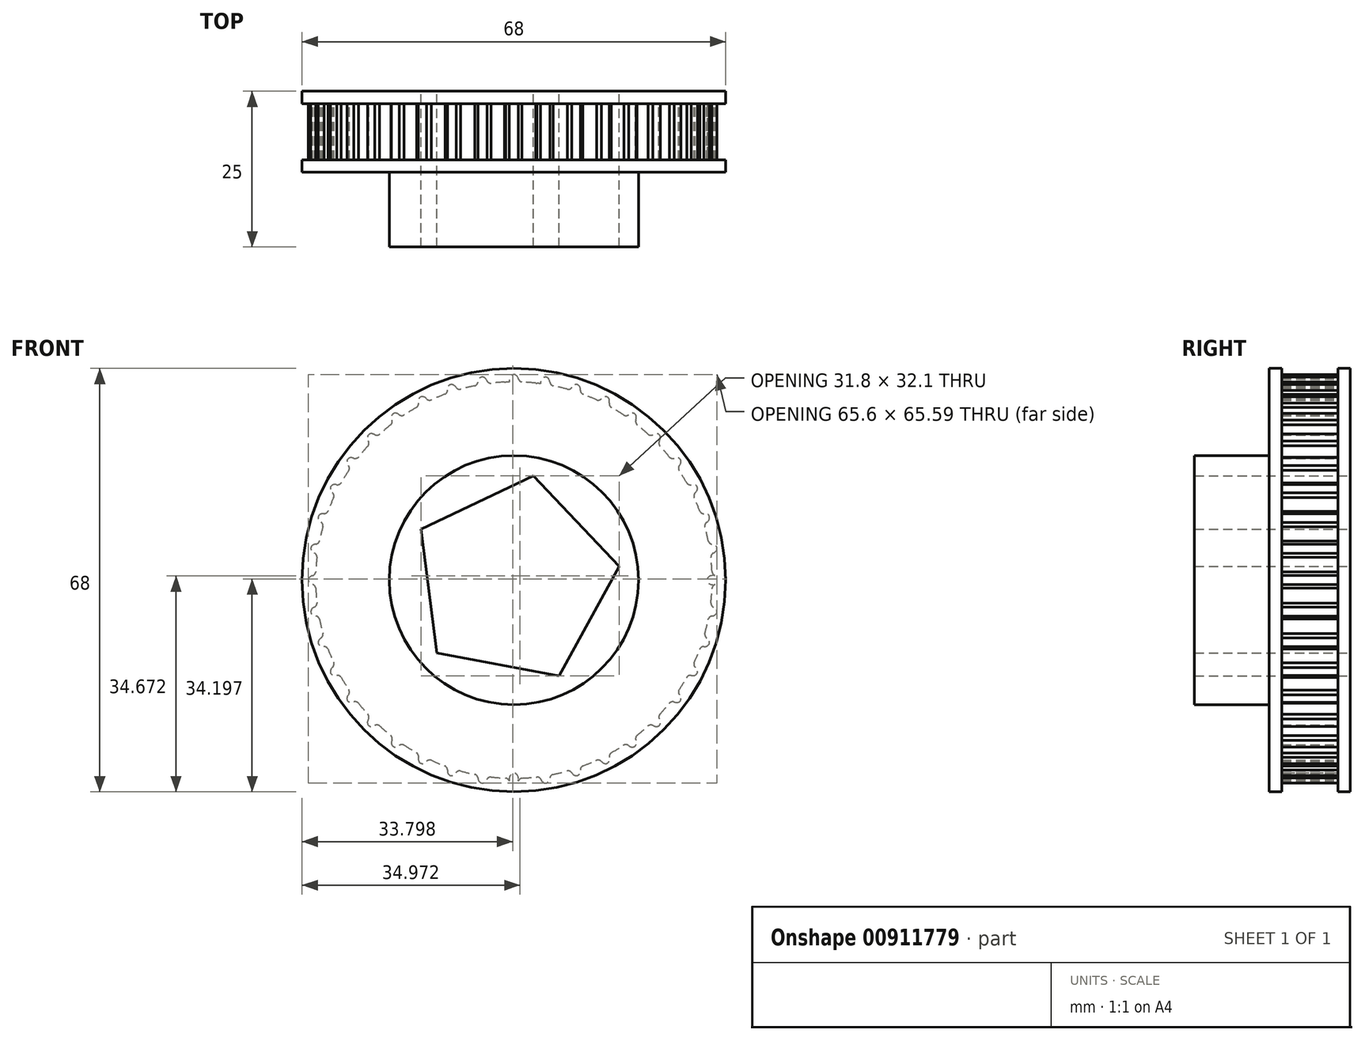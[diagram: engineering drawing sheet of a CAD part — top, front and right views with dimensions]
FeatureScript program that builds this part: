
annotation { "Feature Type Name" : "Feature", "Feature Type Description" : "" }
export const myFeature = defineFeature(function(context is Context, id is Id, definition is map)
    precondition{}
    {
        {
            var Q0;
            Q0=qCreatedBy(makeId("Front.planeOp"),FACE);
            var sketch = newSketch(context, id + "F0", { "sketchPlane" : qUnion([Q0])});
            skCircle(sketch, "E0", {"center": v(0, 0) * mm, "radius": 31.83 * mm});
            skEllipse(sketch, "E1", {"center": v(0, 32) * mm, "majorRadius": 1 * mm, "minorRadius": 0.76 * mm, "majorAxis": v(0, 1)});
            skArc(sketch, "E2", {"start": v(-1.5, 31.8) * mm, "mid": v(-1.02, 31.91) * mm, "end": v(-0.72, 32.3) * mm});
            skArc(sketch, "E3", {"start": v(0.73, 32.28) * mm, "mid": v(1.02, 31.92) * mm, "end": v(1.47, 31.8) * mm});
            skArc(sketch, "E4.1.0", {"start": v(-6.45, 31.17) * mm, "mid": v(-6, 31.36) * mm, "end": v(-5.76, 31.8) * mm});
            skEllipse(sketch, "E4.1.1", {"center": v(-5, 31.6) * mm, "majorRadius": 1 * mm, "minorRadius": 0.76 * mm, "majorAxis": v(-0.16, 0.99)});
            skArc(sketch, "E4.1.2", {"start": v(-4.33, 32) * mm, "mid": v(-3.99, 31.68) * mm, "end": v(-3.52, 31.63) * mm});
            skArc(sketch, "E4.2.0", {"start": v(-11.25, 29.78) * mm, "mid": v(-10.83, 30.04) * mm, "end": v(-10.67, 30.5) * mm});
            skEllipse(sketch, "E4.2.1", {"center": v(-9.89, 30.44) * mm, "majorRadius": 1 * mm, "minorRadius": 0.76 * mm, "majorAxis": v(-0.3, 0.95)});
            skArc(sketch, "E4.2.2", {"start": v(-9.28, 30.93) * mm, "mid": v(-8.9, 30.67) * mm, "end": v(-8.43, 30.7) * mm});
            skArc(sketch, "E4.3.0", {"start": v(-15.77, 27.65) * mm, "mid": v(-15.4, 27.97) * mm, "end": v(-15.3, 28.46) * mm});
            skEllipse(sketch, "E4.3.1", {"center": v(-14.53, 28.52) * mm, "majorRadius": 1 * mm, "minorRadius": 0.76 * mm, "majorAxis": v(-0.45, 0.9)});
            skArc(sketch, "E4.3.2", {"start": v(-14, 29.1) * mm, "mid": v(-13.58, 28.9) * mm, "end": v(-13.12, 29) * mm});
            skArc(sketch, "E4.4.0", {"start": v(-19.9, 24.84) * mm, "mid": v(-19.58, 25.22) * mm, "end": v(-19.57, 25.71) * mm});
            skEllipse(sketch, "E4.4.1", {"center": v(-18.8, 25.9) * mm, "majorRadius": 1 * mm, "minorRadius": 0.76 * mm, "majorAxis": v(-0.59, 0.8)});
            skArc(sketch, "E4.4.2", {"start": v(-18.39, 26.54) * mm, "mid": v(-17.93, 26.42) * mm, "end": v(-17.5, 26.59) * mm});
            skArc(sketch, "E4.5.0", {"start": v(-23.54, 21.42) * mm, "mid": v(-23.29, 21.85) * mm, "end": v(-23.35, 22.33) * mm});
            skEllipse(sketch, "E4.5.1", {"center": v(-22.63, 22.63) * mm, "majorRadius": 1 * mm, "minorRadius": 0.76 * mm, "majorAxis": v(-0.7, 0.7)});
            skArc(sketch, "E4.5.2", {"start": v(-22.31, 23.34) * mm, "mid": v(-21.85, 23.29) * mm, "end": v(-21.44, 23.52) * mm});
            skArc(sketch, "E4.6.0", {"start": v(-26.6, 17.48) * mm, "mid": v(-26.42, 17.93) * mm, "end": v(-26.56, 18.4) * mm});
            skEllipse(sketch, "E4.6.1", {"center": v(-25.9, 18.81) * mm, "majorRadius": 1 * mm, "minorRadius": 0.76 * mm, "majorAxis": v(-0.8, 0.59)});
            skArc(sketch, "E4.6.2", {"start": v(-25.69, 19.56) * mm, "mid": v(-25.22, 19.58) * mm, "end": v(-24.86, 19.88) * mm});
            skArc(sketch, "E4.7.0", {"start": v(-29, 13.1) * mm, "mid": v(-28.9, 13.58) * mm, "end": v(-29.1, 14.03) * mm});
            skEllipse(sketch, "E4.7.1", {"center": v(-28.51, 14.53) * mm, "majorRadius": 1 * mm, "minorRadius": 0.76 * mm, "majorAxis": v(-0.9, 0.45)});
            skArc(sketch, "E4.7.2", {"start": v(-28.43, 15.3) * mm, "mid": v(-27.97, 15.4) * mm, "end": v(-27.66, 15.75) * mm});
            skArc(sketch, "E4.8.0", {"start": v(-30.7, 8.4) * mm, "mid": v(-30.67, 8.9) * mm, "end": v(-30.94, 9.3) * mm});
            skEllipse(sketch, "E4.8.1", {"center": v(-30.44, 9.9) * mm, "majorRadius": 1 * mm, "minorRadius": 0.76 * mm, "majorAxis": v(-0.95, 0.3)});
            skArc(sketch, "E4.8.2", {"start": v(-30.48, 10.67) * mm, "mid": v(-30.04, 10.83) * mm, "end": v(-29.78, 11.22) * mm});
            skArc(sketch, "E4.9.0", {"start": v(-31.64, 3.5) * mm, "mid": v(-31.68, 3.99) * mm, "end": v(-32.02, 4.34) * mm});
            skEllipse(sketch, "E4.9.1", {"center": v(-31.6, 5) * mm, "majorRadius": 1 * mm, "minorRadius": 0.76 * mm, "majorAxis": v(-0.99, 0.16)});
            skArc(sketch, "E4.9.2", {"start": v(-31.77, 5.77) * mm, "mid": v(-31.36, 6) * mm, "end": v(-31.17, 6.43) * mm});
            skArc(sketch, "E4.10.0", {"start": v(-31.8, -1.5) * mm, "mid": v(-31.91, -1.02) * mm, "end": v(-32.3, -0.72) * mm});
            skEllipse(sketch, "E4.10.1", {"center": v(-32, 0) * mm, "majorRadius": 1 * mm, "minorRadius": 0.76 * mm, "majorAxis": v(-1, 0)});
            skArc(sketch, "E4.10.2", {"start": v(-32.28, 0.73) * mm, "mid": v(-31.92, 1.02) * mm, "end": v(-31.8, 1.47) * mm});
            skArc(sketch, "E4.11.0", {"start": v(-31.17, -6.45) * mm, "mid": v(-31.36, -6) * mm, "end": v(-31.8, -5.76) * mm});
            skEllipse(sketch, "E4.11.1", {"center": v(-31.6, -5) * mm, "majorRadius": 1 * mm, "minorRadius": 0.76 * mm, "majorAxis": v(-0.99, -0.16)});
            skArc(sketch, "E4.11.2", {"start": v(-32, -4.33) * mm, "mid": v(-31.68, -3.99) * mm, "end": v(-31.63, -3.52) * mm});
            skArc(sketch, "E4.12.0", {"start": v(-29.78, -11.25) * mm, "mid": v(-30.04, -10.83) * mm, "end": v(-30.5, -10.67) * mm});
            skEllipse(sketch, "E4.12.1", {"center": v(-30.44, -9.89) * mm, "majorRadius": 1 * mm, "minorRadius": 0.76 * mm, "majorAxis": v(-0.95, -0.3)});
            skArc(sketch, "E4.12.2", {"start": v(-30.93, -9.28) * mm, "mid": v(-30.67, -8.9) * mm, "end": v(-30.7, -8.43) * mm});
            skArc(sketch, "E4.13.0", {"start": v(-27.65, -15.77) * mm, "mid": v(-27.97, -15.4) * mm, "end": v(-28.46, -15.3) * mm});
            skEllipse(sketch, "E4.13.1", {"center": v(-28.52, -14.53) * mm, "majorRadius": 1 * mm, "minorRadius": 0.76 * mm, "majorAxis": v(-0.9, -0.45)});
            skArc(sketch, "E4.13.2", {"start": v(-29.1, -14) * mm, "mid": v(-28.9, -13.58) * mm, "end": v(-29, -13.12) * mm});
            skArc(sketch, "E4.14.0", {"start": v(-24.84, -19.9) * mm, "mid": v(-25.22, -19.58) * mm, "end": v(-25.71, -19.57) * mm});
            skEllipse(sketch, "E4.14.1", {"center": v(-25.9, -18.8) * mm, "majorRadius": 1 * mm, "minorRadius": 0.76 * mm, "majorAxis": v(-0.8, -0.59)});
            skArc(sketch, "E4.14.2", {"start": v(-26.54, -18.39) * mm, "mid": v(-26.42, -17.93) * mm, "end": v(-26.59, -17.5) * mm});
            skArc(sketch, "E4.15.0", {"start": v(-21.42, -23.54) * mm, "mid": v(-21.85, -23.29) * mm, "end": v(-22.33, -23.35) * mm});
            skEllipse(sketch, "E4.15.1", {"center": v(-22.63, -22.63) * mm, "majorRadius": 1 * mm, "minorRadius": 0.76 * mm, "majorAxis": v(-0.7, -0.7)});
            skArc(sketch, "E4.15.2", {"start": v(-23.34, -22.31) * mm, "mid": v(-23.29, -21.85) * mm, "end": v(-23.52, -21.44) * mm});
            skArc(sketch, "E4.16.0", {"start": v(-17.48, -26.6) * mm, "mid": v(-17.93, -26.42) * mm, "end": v(-18.4, -26.56) * mm});
            skEllipse(sketch, "E4.16.1", {"center": v(-18.81, -25.9) * mm, "majorRadius": 1 * mm, "minorRadius": 0.76 * mm, "majorAxis": v(-0.59, -0.8)});
            skArc(sketch, "E4.16.2", {"start": v(-19.56, -25.69) * mm, "mid": v(-19.58, -25.22) * mm, "end": v(-19.88, -24.86) * mm});
            skArc(sketch, "E4.17.0", {"start": v(-13.1, -29) * mm, "mid": v(-13.58, -28.9) * mm, "end": v(-14.03, -29.1) * mm});
            skEllipse(sketch, "E4.17.1", {"center": v(-14.53, -28.51) * mm, "majorRadius": 1 * mm, "minorRadius": 0.76 * mm, "majorAxis": v(-0.45, -0.9)});
            skArc(sketch, "E4.17.2", {"start": v(-15.3, -28.43) * mm, "mid": v(-15.4, -27.97) * mm, "end": v(-15.75, -27.66) * mm});
            skArc(sketch, "E4.18.0", {"start": v(-8.4, -30.7) * mm, "mid": v(-8.9, -30.67) * mm, "end": v(-9.3, -30.94) * mm});
            skEllipse(sketch, "E4.18.1", {"center": v(-9.9, -30.44) * mm, "majorRadius": 1 * mm, "minorRadius": 0.76 * mm, "majorAxis": v(-0.3, -0.95)});
            skArc(sketch, "E4.18.2", {"start": v(-10.67, -30.48) * mm, "mid": v(-10.83, -30.04) * mm, "end": v(-11.22, -29.78) * mm});
            skArc(sketch, "E4.19.0", {"start": v(-3.5, -31.64) * mm, "mid": v(-3.99, -31.68) * mm, "end": v(-4.34, -32.02) * mm});
            skEllipse(sketch, "E4.19.1", {"center": v(-5, -31.6) * mm, "majorRadius": 1 * mm, "minorRadius": 0.76 * mm, "majorAxis": v(-0.16, -0.99)});
            skArc(sketch, "E4.19.2", {"start": v(-5.77, -31.77) * mm, "mid": v(-6, -31.36) * mm, "end": v(-6.43, -31.17) * mm});
            skArc(sketch, "E4.20.0", {"start": v(1.5, -31.8) * mm, "mid": v(1.02, -31.91) * mm, "end": v(0.72, -32.3) * mm});
            skEllipse(sketch, "E4.20.1", {"center": v(0, -32) * mm, "majorRadius": 1 * mm, "minorRadius": 0.76 * mm, "majorAxis": v(0, -1)});
            skArc(sketch, "E4.20.2", {"start": v(-0.73, -32.28) * mm, "mid": v(-1.02, -31.92) * mm, "end": v(-1.47, -31.8) * mm});
            skArc(sketch, "E4.21.0", {"start": v(6.45, -31.17) * mm, "mid": v(6, -31.36) * mm, "end": v(5.76, -31.8) * mm});
            skEllipse(sketch, "E4.21.1", {"center": v(5, -31.6) * mm, "majorRadius": 1 * mm, "minorRadius": 0.76 * mm, "majorAxis": v(0.16, -0.99)});
            skArc(sketch, "E4.21.2", {"start": v(4.33, -32) * mm, "mid": v(3.99, -31.68) * mm, "end": v(3.52, -31.63) * mm});
            skArc(sketch, "E4.22.0", {"start": v(11.25, -29.78) * mm, "mid": v(10.83, -30.04) * mm, "end": v(10.67, -30.5) * mm});
            skEllipse(sketch, "E4.22.1", {"center": v(9.89, -30.44) * mm, "majorRadius": 1 * mm, "minorRadius": 0.76 * mm, "majorAxis": v(0.3, -0.95)});
            skArc(sketch, "E4.22.2", {"start": v(9.28, -30.93) * mm, "mid": v(8.9, -30.67) * mm, "end": v(8.43, -30.7) * mm});
            skArc(sketch, "E4.23.0", {"start": v(15.77, -27.65) * mm, "mid": v(15.4, -27.97) * mm, "end": v(15.3, -28.46) * mm});
            skEllipse(sketch, "E4.23.1", {"center": v(14.53, -28.52) * mm, "majorRadius": 1 * mm, "minorRadius": 0.76 * mm, "majorAxis": v(0.45, -0.9)});
            skArc(sketch, "E4.23.2", {"start": v(14, -29.1) * mm, "mid": v(13.58, -28.9) * mm, "end": v(13.12, -29) * mm});
            skArc(sketch, "E4.24.0", {"start": v(19.9, -24.84) * mm, "mid": v(19.58, -25.22) * mm, "end": v(19.57, -25.71) * mm});
            skEllipse(sketch, "E4.24.1", {"center": v(18.8, -25.9) * mm, "majorRadius": 1 * mm, "minorRadius": 0.76 * mm, "majorAxis": v(0.59, -0.8)});
            skArc(sketch, "E4.24.2", {"start": v(18.39, -26.54) * mm, "mid": v(17.93, -26.42) * mm, "end": v(17.5, -26.59) * mm});
            skArc(sketch, "E4.25.0", {"start": v(23.54, -21.42) * mm, "mid": v(23.29, -21.85) * mm, "end": v(23.35, -22.33) * mm});
            skEllipse(sketch, "E4.25.1", {"center": v(22.63, -22.63) * mm, "majorRadius": 1 * mm, "minorRadius": 0.76 * mm, "majorAxis": v(0.7, -0.7)});
            skArc(sketch, "E4.25.2", {"start": v(22.31, -23.34) * mm, "mid": v(21.85, -23.29) * mm, "end": v(21.44, -23.52) * mm});
            skArc(sketch, "E4.26.0", {"start": v(26.6, -17.48) * mm, "mid": v(26.42, -17.93) * mm, "end": v(26.56, -18.4) * mm});
            skEllipse(sketch, "E4.26.1", {"center": v(25.9, -18.81) * mm, "majorRadius": 1 * mm, "minorRadius": 0.76 * mm, "majorAxis": v(0.8, -0.59)});
            skArc(sketch, "E4.26.2", {"start": v(25.69, -19.56) * mm, "mid": v(25.22, -19.58) * mm, "end": v(24.86, -19.88) * mm});
            skArc(sketch, "E4.27.0", {"start": v(29, -13.1) * mm, "mid": v(28.9, -13.58) * mm, "end": v(29.1, -14.03) * mm});
            skEllipse(sketch, "E4.27.1", {"center": v(28.51, -14.53) * mm, "majorRadius": 1 * mm, "minorRadius": 0.76 * mm, "majorAxis": v(0.9, -0.45)});
            skArc(sketch, "E4.27.2", {"start": v(28.43, -15.3) * mm, "mid": v(27.97, -15.4) * mm, "end": v(27.66, -15.75) * mm});
            skArc(sketch, "E4.28.0", {"start": v(30.7, -8.4) * mm, "mid": v(30.67, -8.9) * mm, "end": v(30.94, -9.3) * mm});
            skEllipse(sketch, "E4.28.1", {"center": v(30.44, -9.9) * mm, "majorRadius": 1 * mm, "minorRadius": 0.76 * mm, "majorAxis": v(0.95, -0.3)});
            skArc(sketch, "E4.28.2", {"start": v(30.48, -10.67) * mm, "mid": v(30.04, -10.83) * mm, "end": v(29.78, -11.22) * mm});
            skArc(sketch, "E4.29.0", {"start": v(31.64, -3.5) * mm, "mid": v(31.68, -3.99) * mm, "end": v(32.02, -4.34) * mm});
            skEllipse(sketch, "E4.29.1", {"center": v(31.6, -5) * mm, "majorRadius": 1 * mm, "minorRadius": 0.76 * mm, "majorAxis": v(0.99, -0.16)});
            skArc(sketch, "E4.29.2", {"start": v(31.77, -5.77) * mm, "mid": v(31.36, -6) * mm, "end": v(31.17, -6.43) * mm});
            skArc(sketch, "E4.30.0", {"start": v(31.8, 1.5) * mm, "mid": v(31.91, 1.02) * mm, "end": v(32.3, 0.72) * mm});
            skEllipse(sketch, "E4.30.1", {"center": v(32, 0) * mm, "majorRadius": 1 * mm, "minorRadius": 0.76 * mm, "majorAxis": v(1, 0)});
            skArc(sketch, "E4.30.2", {"start": v(32.28, -0.73) * mm, "mid": v(31.92, -1.02) * mm, "end": v(31.8, -1.47) * mm});
            skArc(sketch, "E4.31.0", {"start": v(31.17, 6.45) * mm, "mid": v(31.36, 6) * mm, "end": v(31.8, 5.76) * mm});
            skEllipse(sketch, "E4.31.1", {"center": v(31.6, 5) * mm, "majorRadius": 1 * mm, "minorRadius": 0.76 * mm, "majorAxis": v(0.99, 0.16)});
            skArc(sketch, "E4.31.2", {"start": v(32, 4.33) * mm, "mid": v(31.68, 3.99) * mm, "end": v(31.63, 3.52) * mm});
            skArc(sketch, "E4.32.0", {"start": v(29.78, 11.25) * mm, "mid": v(30.04, 10.83) * mm, "end": v(30.5, 10.67) * mm});
            skEllipse(sketch, "E4.32.1", {"center": v(30.44, 9.89) * mm, "majorRadius": 1 * mm, "minorRadius": 0.76 * mm, "majorAxis": v(0.95, 0.3)});
            skArc(sketch, "E4.32.2", {"start": v(30.93, 9.28) * mm, "mid": v(30.67, 8.9) * mm, "end": v(30.7, 8.43) * mm});
            skArc(sketch, "E4.33.0", {"start": v(27.65, 15.77) * mm, "mid": v(27.97, 15.4) * mm, "end": v(28.46, 15.3) * mm});
            skEllipse(sketch, "E4.33.1", {"center": v(28.52, 14.53) * mm, "majorRadius": 1 * mm, "minorRadius": 0.76 * mm, "majorAxis": v(0.9, 0.45)});
            skArc(sketch, "E4.33.2", {"start": v(29.1, 14) * mm, "mid": v(28.9, 13.58) * mm, "end": v(29, 13.12) * mm});
            skArc(sketch, "E4.34.0", {"start": v(24.84, 19.9) * mm, "mid": v(25.22, 19.58) * mm, "end": v(25.71, 19.57) * mm});
            skEllipse(sketch, "E4.34.1", {"center": v(25.9, 18.8) * mm, "majorRadius": 1 * mm, "minorRadius": 0.76 * mm, "majorAxis": v(0.8, 0.59)});
            skArc(sketch, "E4.34.2", {"start": v(26.54, 18.39) * mm, "mid": v(26.42, 17.93) * mm, "end": v(26.59, 17.5) * mm});
            skArc(sketch, "E4.35.0", {"start": v(21.42, 23.54) * mm, "mid": v(21.85, 23.29) * mm, "end": v(22.33, 23.35) * mm});
            skEllipse(sketch, "E4.35.1", {"center": v(22.63, 22.63) * mm, "majorRadius": 1 * mm, "minorRadius": 0.76 * mm, "majorAxis": v(0.7, 0.7)});
            skArc(sketch, "E4.35.2", {"start": v(23.34, 22.31) * mm, "mid": v(23.29, 21.85) * mm, "end": v(23.52, 21.44) * mm});
            skArc(sketch, "E4.36.0", {"start": v(17.48, 26.6) * mm, "mid": v(17.93, 26.42) * mm, "end": v(18.4, 26.56) * mm});
            skEllipse(sketch, "E4.36.1", {"center": v(18.81, 25.9) * mm, "majorRadius": 1 * mm, "minorRadius": 0.76 * mm, "majorAxis": v(0.59, 0.8)});
            skArc(sketch, "E4.36.2", {"start": v(19.56, 25.69) * mm, "mid": v(19.58, 25.22) * mm, "end": v(19.88, 24.86) * mm});
            skArc(sketch, "E4.37.0", {"start": v(13.1, 29) * mm, "mid": v(13.58, 28.9) * mm, "end": v(14.03, 29.1) * mm});
            skEllipse(sketch, "E4.37.1", {"center": v(14.53, 28.51) * mm, "majorRadius": 1 * mm, "minorRadius": 0.76 * mm, "majorAxis": v(0.45, 0.9)});
            skArc(sketch, "E4.37.2", {"start": v(15.3, 28.43) * mm, "mid": v(15.4, 27.97) * mm, "end": v(15.75, 27.66) * mm});
            skArc(sketch, "E4.38.0", {"start": v(8.4, 30.7) * mm, "mid": v(8.9, 30.67) * mm, "end": v(9.3, 30.94) * mm});
            skEllipse(sketch, "E4.38.1", {"center": v(9.9, 30.44) * mm, "majorRadius": 1 * mm, "minorRadius": 0.76 * mm, "majorAxis": v(0.3, 0.95)});
            skArc(sketch, "E4.38.2", {"start": v(10.67, 30.48) * mm, "mid": v(10.83, 30.04) * mm, "end": v(11.22, 29.78) * mm});
            skArc(sketch, "E4.39.0", {"start": v(3.5, 31.64) * mm, "mid": v(3.99, 31.68) * mm, "end": v(4.34, 32.02) * mm});
            skEllipse(sketch, "E4.39.1", {"center": v(5, 31.6) * mm, "majorRadius": 1 * mm, "minorRadius": 0.76 * mm, "majorAxis": v(0.16, 0.99)});
            skArc(sketch, "E4.39.2", {"start": v(5.77, 31.77) * mm, "mid": v(6, 31.36) * mm, "end": v(6.43, 31.17) * mm});
            skSolve(sketch);
        }
        {
            var Q0;
            {var subQ0=sQuery(id+"F0.wireOp",EDGE,"E4.9.1");var subQ1=sQuery(id+"F0.wireOp",EDGE,"E0");var subQ2=makeQuery(id+"F0.imprint","INTERSECT",VERTEX,{"disambiguationData":[OD(0.0)],"derivedFrom":[subQ1,subQ0]});Q0=makeQuery(id+"F0.imprint","IMPRINT",FACE,{"disambiguationData":[TD([[makeQuery(id+"F0.imprint","IMPRINT",EDGE,{"disambiguationData":[TD([[subQ2,-1.0]])],"derivedFrom":subQ1}),-1.0]])]});}
            var Q1;
            {var subQ1=sQuery(id+"F0.wireOp",EDGE,"E0");var subQ208=sQuery(id+"F0.wireOp",EDGE,"E4.30.0");var subQ210=makeQuery(id+"F0.imprint","INTERSECT",VERTEX,{"disambiguationData":[OD(1.0)],"derivedFrom":[subQ1,subQ208]});Q1=makeQuery(id+"F0.imprint","IMPRINT",FACE,{"disambiguationData":[TD([[makeQuery(id+"F0.imprint","IMPRINT",EDGE,{"disambiguationData":[TD([[subQ210,1.0]])],"derivedFrom":subQ1}),1.0]])]});}
            var Q2;
            {var subQ0=sQuery(id+"F0.wireOp",EDGE,"E4.4.1");var subQ1=sQuery(id+"F0.wireOp",EDGE,"E0");var subQ2=makeQuery(id+"F0.imprint","INTERSECT",VERTEX,{"disambiguationData":[OD(0.0)],"derivedFrom":[subQ1,subQ0]});Q2=makeQuery(id+"F0.imprint","IMPRINT",FACE,{"disambiguationData":[TD([[makeQuery(id+"F0.imprint","IMPRINT",EDGE,{"disambiguationData":[TD([[subQ2,-1.0]])],"derivedFrom":subQ1}),1.0]])]});}
            var Q3;
            {var subQ0=sQuery(id+"F0.wireOp",EDGE,"E4.8.0");var subQ1=sQuery(id+"F0.wireOp",EDGE,"E0");var subQ2=makeQuery(id+"F0.imprint","INTERSECT",VERTEX,{"disambiguationData":[OD(1.0)],"derivedFrom":[subQ1,subQ0]});Q3=makeQuery(id+"F0.imprint","IMPRINT",FACE,{"disambiguationData":[TD([[makeQuery(id+"F0.imprint","IMPRINT",EDGE,{"disambiguationData":[TD([[subQ2,1.0]])],"derivedFrom":subQ1}),-1.0]])]});}
            var Q4;
            {var subQ0=sQuery(id+"F0.wireOp",EDGE,"E4.32.1");var subQ1=sQuery(id+"F0.wireOp",EDGE,"E0");var subQ2=makeQuery(id+"F0.imprint","INTERSECT",VERTEX,{"disambiguationData":[OD(0.0)],"derivedFrom":[subQ1,subQ0]});Q4=makeQuery(id+"F0.imprint","IMPRINT",FACE,{"disambiguationData":[TD([[makeQuery(id+"F0.imprint","IMPRINT",EDGE,{"disambiguationData":[TD([[subQ2,-1.0]])],"derivedFrom":subQ1}),-1.0]])]});}
            var Q5;
            {var subQ0=sQuery(id+"F0.wireOp",EDGE,"E4.30.1");var subQ1=sQuery(id+"F0.wireOp",EDGE,"E0");var subQ2=makeQuery(id+"F0.imprint","INTERSECT",VERTEX,{"disambiguationData":[OD(0.0)],"derivedFrom":[subQ1,subQ0]});Q5=makeQuery(id+"F0.imprint","IMPRINT",FACE,{"disambiguationData":[TD([[makeQuery(id+"F0.imprint","IMPRINT",EDGE,{"disambiguationData":[TD([[subQ2,1.0]])],"derivedFrom":subQ1}),1.0]])]});}
            var Q6;
            {var subQ0=sQuery(id+"F0.wireOp",EDGE,"E4.36.1");var subQ1=sQuery(id+"F0.wireOp",EDGE,"E0");var subQ2=makeQuery(id+"F0.imprint","INTERSECT",VERTEX,{"disambiguationData":[OD(0.0)],"derivedFrom":[subQ1,subQ0]});Q6=makeQuery(id+"F0.imprint","IMPRINT",FACE,{"disambiguationData":[TD([[makeQuery(id+"F0.imprint","IMPRINT",EDGE,{"disambiguationData":[TD([[subQ2,-1.0]])],"derivedFrom":subQ1}),1.0]])]});}
            var Q7;
            {var subQ0=sQuery(id+"F0.wireOp",EDGE,"E4.10.1");var subQ1=sQuery(id+"F0.wireOp",EDGE,"E0");var subQ2=makeQuery(id+"F0.imprint","INTERSECT",VERTEX,{"disambiguationData":[OD(0.0)],"derivedFrom":[subQ1,subQ0]});Q7=makeQuery(id+"F0.imprint","IMPRINT",FACE,{"disambiguationData":[TD([[makeQuery(id+"F0.imprint","IMPRINT",EDGE,{"disambiguationData":[TD([[subQ2,-1.0]])],"derivedFrom":subQ1}),1.0]])]});}
            var Q8;
            {var subQ0=sQuery(id+"F0.wireOp",EDGE,"E4.6.1");var subQ1=sQuery(id+"F0.wireOp",EDGE,"E0");var subQ2=makeQuery(id+"F0.imprint","INTERSECT",VERTEX,{"disambiguationData":[OD(0.0)],"derivedFrom":[subQ1,subQ0]});Q8=makeQuery(id+"F0.imprint","IMPRINT",FACE,{"disambiguationData":[TD([[makeQuery(id+"F0.imprint","IMPRINT",EDGE,{"disambiguationData":[TD([[subQ2,-1.0]])],"derivedFrom":subQ1}),1.0]])]});}
            var Q9;
            {var subQ0=sQuery(id+"F0.wireOp",EDGE,"E4.26.1");var subQ1=sQuery(id+"F0.wireOp",EDGE,"E0");var subQ2=makeQuery(id+"F0.imprint","INTERSECT",VERTEX,{"disambiguationData":[OD(0.0)],"derivedFrom":[subQ1,subQ0]});Q9=makeQuery(id+"F0.imprint","IMPRINT",FACE,{"disambiguationData":[TD([[makeQuery(id+"F0.imprint","IMPRINT",EDGE,{"disambiguationData":[TD([[subQ2,-1.0]])],"derivedFrom":subQ1}),1.0]])]});}
            var Q10;
            {var subQ0=sQuery(id+"F0.wireOp",EDGE,"E4.21.1");var subQ1=sQuery(id+"F0.wireOp",EDGE,"E0");var subQ2=makeQuery(id+"F0.imprint","INTERSECT",VERTEX,{"disambiguationData":[OD(0.0)],"derivedFrom":[subQ1,subQ0]});Q10=makeQuery(id+"F0.imprint","IMPRINT",FACE,{"disambiguationData":[TD([[makeQuery(id+"F0.imprint","IMPRINT",EDGE,{"disambiguationData":[TD([[subQ2,-1.0]])],"derivedFrom":subQ1}),1.0]])]});}
            var Q11;
            {var subQ0=sQuery(id+"F0.wireOp",EDGE,"E4.18.1");var subQ1=sQuery(id+"F0.wireOp",EDGE,"E0");var subQ2=makeQuery(id+"F0.imprint","INTERSECT",VERTEX,{"disambiguationData":[OD(0.0)],"derivedFrom":[subQ1,subQ0]});Q11=makeQuery(id+"F0.imprint","IMPRINT",FACE,{"disambiguationData":[TD([[makeQuery(id+"F0.imprint","IMPRINT",EDGE,{"disambiguationData":[TD([[subQ2,-1.0]])],"derivedFrom":subQ1}),-1.0]])]});}
            var Q12;
            {var subQ0=sQuery(id+"F0.wireOp",EDGE,"E1");var subQ1=sQuery(id+"F0.wireOp",EDGE,"E0");var subQ2=makeQuery(id+"F0.imprint","INTERSECT",VERTEX,{"disambiguationData":[OD(0.0)],"derivedFrom":[subQ1,subQ0]});Q12=makeQuery(id+"F0.imprint","IMPRINT",FACE,{"disambiguationData":[TD([[makeQuery(id+"F0.imprint","IMPRINT",EDGE,{"disambiguationData":[TD([[subQ2,-1.0]])],"derivedFrom":subQ1}),1.0]])]});}
            var Q13;
            {var subQ0=sQuery(id+"F0.wireOp",EDGE,"E4.33.1");var subQ1=sQuery(id+"F0.wireOp",EDGE,"E0");var subQ2=makeQuery(id+"F0.imprint","INTERSECT",VERTEX,{"disambiguationData":[OD(0.0)],"derivedFrom":[subQ1,subQ0]});Q13=makeQuery(id+"F0.imprint","IMPRINT",FACE,{"disambiguationData":[TD([[makeQuery(id+"F0.imprint","IMPRINT",EDGE,{"disambiguationData":[TD([[subQ2,-1.0]])],"derivedFrom":subQ1}),1.0]])]});}
            var Q14;
            {var subQ0=sQuery(id+"F0.wireOp",EDGE,"E4.34.1");var subQ1=sQuery(id+"F0.wireOp",EDGE,"E0");var subQ2=makeQuery(id+"F0.imprint","INTERSECT",VERTEX,{"disambiguationData":[OD(0.0)],"derivedFrom":[subQ1,subQ0]});Q14=makeQuery(id+"F0.imprint","IMPRINT",FACE,{"disambiguationData":[TD([[makeQuery(id+"F0.imprint","IMPRINT",EDGE,{"disambiguationData":[TD([[subQ2,-1.0]])],"derivedFrom":subQ1}),1.0]])]});}
            var Q15;
            {var subQ0=sQuery(id+"F0.wireOp",EDGE,"E4.17.0");var subQ1=sQuery(id+"F0.wireOp",EDGE,"E0");var subQ2=makeQuery(id+"F0.imprint","INTERSECT",VERTEX,{"disambiguationData":[OD(1.0)],"derivedFrom":[subQ1,subQ0]});Q15=makeQuery(id+"F0.imprint","IMPRINT",FACE,{"disambiguationData":[TD([[makeQuery(id+"F0.imprint","IMPRINT",EDGE,{"disambiguationData":[TD([[subQ2,1.0]])],"derivedFrom":subQ1}),-1.0]])]});}
            var Q16;
            {var subQ0=sQuery(id+"F0.wireOp",EDGE,"E4.39.1");var subQ1=sQuery(id+"F0.wireOp",EDGE,"E0");var subQ2=makeQuery(id+"F0.imprint","INTERSECT",VERTEX,{"disambiguationData":[OD(0.0)],"derivedFrom":[subQ1,subQ0]});Q16=makeQuery(id+"F0.imprint","IMPRINT",FACE,{"disambiguationData":[TD([[makeQuery(id+"F0.imprint","IMPRINT",EDGE,{"disambiguationData":[TD([[subQ2,-1.0]])],"derivedFrom":subQ1}),1.0]])]});}
            var Q17;
            {var subQ0=sQuery(id+"F0.wireOp",EDGE,"E4.7.1");var subQ1=sQuery(id+"F0.wireOp",EDGE,"E0");var subQ2=makeQuery(id+"F0.imprint","INTERSECT",VERTEX,{"disambiguationData":[OD(0.0)],"derivedFrom":[subQ1,subQ0]});Q17=makeQuery(id+"F0.imprint","IMPRINT",FACE,{"disambiguationData":[TD([[makeQuery(id+"F0.imprint","IMPRINT",EDGE,{"disambiguationData":[TD([[subQ2,-1.0]])],"derivedFrom":subQ1}),-1.0]])]});}
            var Q18;
            {var subQ0=sQuery(id+"F0.wireOp",EDGE,"E4.33.1");var subQ1=sQuery(id+"F0.wireOp",EDGE,"E0");var subQ2=makeQuery(id+"F0.imprint","INTERSECT",VERTEX,{"disambiguationData":[OD(0.0)],"derivedFrom":[subQ1,subQ0]});Q18=makeQuery(id+"F0.imprint","IMPRINT",FACE,{"disambiguationData":[TD([[makeQuery(id+"F0.imprint","IMPRINT",EDGE,{"disambiguationData":[TD([[subQ2,-1.0]])],"derivedFrom":subQ1}),-1.0]])]});}
            var Q19;
            {var subQ0=sQuery(id+"F0.wireOp",EDGE,"E4.19.1");var subQ1=sQuery(id+"F0.wireOp",EDGE,"E0");var subQ2=makeQuery(id+"F0.imprint","INTERSECT",VERTEX,{"disambiguationData":[OD(0.0)],"derivedFrom":[subQ1,subQ0]});Q19=makeQuery(id+"F0.imprint","IMPRINT",FACE,{"disambiguationData":[TD([[makeQuery(id+"F0.imprint","IMPRINT",EDGE,{"disambiguationData":[TD([[subQ2,-1.0]])],"derivedFrom":subQ1}),-1.0]])]});}
            var Q20;
            {var subQ0=sQuery(id+"F0.wireOp",EDGE,"E4.19.1");var subQ1=sQuery(id+"F0.wireOp",EDGE,"E0");var subQ2=makeQuery(id+"F0.imprint","INTERSECT",VERTEX,{"disambiguationData":[OD(0.0)],"derivedFrom":[subQ1,subQ0]});Q20=makeQuery(id+"F0.imprint","IMPRINT",FACE,{"disambiguationData":[TD([[makeQuery(id+"F0.imprint","IMPRINT",EDGE,{"disambiguationData":[TD([[subQ2,-1.0]])],"derivedFrom":subQ1}),1.0]])]});}
            var Q21;
            {var subQ0=sQuery(id+"F0.wireOp",EDGE,"E4.6.2");var subQ1=sQuery(id+"F0.wireOp",EDGE,"E0");var subQ2=makeQuery(id+"F0.imprint","INTERSECT",VERTEX,{"derivedFrom":[subQ1,subQ0]});Q21=makeQuery(id+"F0.imprint","IMPRINT",FACE,{"disambiguationData":[TD([[makeQuery(id+"F0.imprint","IMPRINT",EDGE,{"disambiguationData":[TD([[subQ2,-1.0]])],"derivedFrom":subQ1}),-1.0]])]});}
            var Q22;
            {var subQ0=sQuery(id+"F0.wireOp",EDGE,"E4.36.1");var subQ1=sQuery(id+"F0.wireOp",EDGE,"E0");var subQ2=makeQuery(id+"F0.imprint","INTERSECT",VERTEX,{"disambiguationData":[OD(0.0)],"derivedFrom":[subQ1,subQ0]});Q22=makeQuery(id+"F0.imprint","IMPRINT",FACE,{"disambiguationData":[TD([[makeQuery(id+"F0.imprint","IMPRINT",EDGE,{"disambiguationData":[TD([[subQ2,-1.0]])],"derivedFrom":subQ1}),-1.0]])]});}
            var Q23;
            {var subQ0=sQuery(id+"F0.wireOp",EDGE,"E4.37.1");var subQ1=sQuery(id+"F0.wireOp",EDGE,"E0");var subQ2=makeQuery(id+"F0.imprint","INTERSECT",VERTEX,{"disambiguationData":[OD(0.0)],"derivedFrom":[subQ1,subQ0]});Q23=makeQuery(id+"F0.imprint","IMPRINT",FACE,{"disambiguationData":[TD([[makeQuery(id+"F0.imprint","IMPRINT",EDGE,{"disambiguationData":[TD([[subQ2,-1.0]])],"derivedFrom":subQ1}),-1.0]])]});}
            var Q24;
            {var subQ0=sQuery(id+"F0.wireOp",EDGE,"E4.27.1");var subQ1=sQuery(id+"F0.wireOp",EDGE,"E0");var subQ2=makeQuery(id+"F0.imprint","INTERSECT",VERTEX,{"disambiguationData":[OD(0.0)],"derivedFrom":[subQ1,subQ0]});Q24=makeQuery(id+"F0.imprint","IMPRINT",FACE,{"disambiguationData":[TD([[makeQuery(id+"F0.imprint","IMPRINT",EDGE,{"disambiguationData":[TD([[subQ2,-1.0]])],"derivedFrom":subQ1}),1.0]])]});}
            var Q25;
            {var subQ0=sQuery(id+"F0.wireOp",EDGE,"E4.26.1");var subQ1=sQuery(id+"F0.wireOp",EDGE,"E0");var subQ2=makeQuery(id+"F0.imprint","INTERSECT",VERTEX,{"disambiguationData":[OD(0.0)],"derivedFrom":[subQ1,subQ0]});Q25=makeQuery(id+"F0.imprint","IMPRINT",FACE,{"disambiguationData":[TD([[makeQuery(id+"F0.imprint","IMPRINT",EDGE,{"disambiguationData":[TD([[subQ2,-1.0]])],"derivedFrom":subQ1}),-1.0]])]});}
            var Q26;
            {var subQ0=sQuery(id+"F0.wireOp",EDGE,"E4.10.1");var subQ1=sQuery(id+"F0.wireOp",EDGE,"E0");var subQ2=makeQuery(id+"F0.imprint","INTERSECT",VERTEX,{"disambiguationData":[OD(0.0)],"derivedFrom":[subQ1,subQ0]});Q26=makeQuery(id+"F0.imprint","IMPRINT",FACE,{"disambiguationData":[TD([[makeQuery(id+"F0.imprint","IMPRINT",EDGE,{"disambiguationData":[TD([[subQ2,-1.0]])],"derivedFrom":subQ1}),-1.0]])]});}
            var Q27;
            {var subQ0=sQuery(id+"F0.wireOp",EDGE,"E4.15.1");var subQ1=sQuery(id+"F0.wireOp",EDGE,"E0");var subQ2=makeQuery(id+"F0.imprint","INTERSECT",VERTEX,{"disambiguationData":[OD(0.0)],"derivedFrom":[subQ1,subQ0]});Q27=makeQuery(id+"F0.imprint","IMPRINT",FACE,{"disambiguationData":[TD([[makeQuery(id+"F0.imprint","IMPRINT",EDGE,{"disambiguationData":[TD([[subQ2,-1.0]])],"derivedFrom":subQ1}),-1.0]])]});}
            var Q28;
            {var subQ0=sQuery(id+"F0.wireOp",EDGE,"E4.20.1");var subQ1=sQuery(id+"F0.wireOp",EDGE,"E0");var subQ2=makeQuery(id+"F0.imprint","INTERSECT",VERTEX,{"disambiguationData":[OD(0.0)],"derivedFrom":[subQ1,subQ0]});Q28=makeQuery(id+"F0.imprint","IMPRINT",FACE,{"disambiguationData":[TD([[makeQuery(id+"F0.imprint","IMPRINT",EDGE,{"disambiguationData":[TD([[subQ2,-1.0]])],"derivedFrom":subQ1}),1.0]])]});}
            var Q29;
            {var subQ0=sQuery(id+"F0.wireOp",EDGE,"E4.31.1");var subQ1=sQuery(id+"F0.wireOp",EDGE,"E0");var subQ2=makeQuery(id+"F0.imprint","INTERSECT",VERTEX,{"disambiguationData":[OD(0.0)],"derivedFrom":[subQ1,subQ0]});Q29=makeQuery(id+"F0.imprint","IMPRINT",FACE,{"disambiguationData":[TD([[makeQuery(id+"F0.imprint","IMPRINT",EDGE,{"disambiguationData":[TD([[subQ2,-1.0]])],"derivedFrom":subQ1}),-1.0]])]});}
            var Q30;
            {var subQ0=sQuery(id+"F0.wireOp",EDGE,"E4.21.1");var subQ1=sQuery(id+"F0.wireOp",EDGE,"E0");var subQ2=makeQuery(id+"F0.imprint","INTERSECT",VERTEX,{"disambiguationData":[OD(0.0)],"derivedFrom":[subQ1,subQ0]});Q30=makeQuery(id+"F0.imprint","IMPRINT",FACE,{"disambiguationData":[TD([[makeQuery(id+"F0.imprint","IMPRINT",EDGE,{"disambiguationData":[TD([[subQ2,-1.0]])],"derivedFrom":subQ1}),-1.0]])]});}
            var Q31;
            {var subQ0=sQuery(id+"F0.wireOp",EDGE,"E4.18.1");var subQ1=sQuery(id+"F0.wireOp",EDGE,"E0");var subQ2=makeQuery(id+"F0.imprint","INTERSECT",VERTEX,{"disambiguationData":[OD(0.0)],"derivedFrom":[subQ1,subQ0]});Q31=makeQuery(id+"F0.imprint","IMPRINT",FACE,{"disambiguationData":[TD([[makeQuery(id+"F0.imprint","IMPRINT",EDGE,{"disambiguationData":[TD([[subQ2,-1.0]])],"derivedFrom":subQ1}),1.0]])]});}
            var Q32;
            {var subQ0=sQuery(id+"F0.wireOp",EDGE,"E4.37.1");var subQ1=sQuery(id+"F0.wireOp",EDGE,"E0");var subQ2=makeQuery(id+"F0.imprint","INTERSECT",VERTEX,{"disambiguationData":[OD(0.0)],"derivedFrom":[subQ1,subQ0]});Q32=makeQuery(id+"F0.imprint","IMPRINT",FACE,{"disambiguationData":[TD([[makeQuery(id+"F0.imprint","IMPRINT",EDGE,{"disambiguationData":[TD([[subQ2,-1.0]])],"derivedFrom":subQ1}),1.0]])]});}
            var Q33;
            {var subQ0=sQuery(id+"F0.wireOp",EDGE,"E4.1.1");var subQ1=sQuery(id+"F0.wireOp",EDGE,"E0");var subQ2=makeQuery(id+"F0.imprint","INTERSECT",VERTEX,{"disambiguationData":[OD(0.0)],"derivedFrom":[subQ1,subQ0]});Q33=makeQuery(id+"F0.imprint","IMPRINT",FACE,{"disambiguationData":[TD([[makeQuery(id+"F0.imprint","IMPRINT",EDGE,{"disambiguationData":[TD([[subQ2,-1.0]])],"derivedFrom":subQ1}),-1.0]])]});}
            var Q34;
            {var subQ0=sQuery(id+"F0.wireOp",EDGE,"E4.12.1");var subQ1=sQuery(id+"F0.wireOp",EDGE,"E0");var subQ2=makeQuery(id+"F0.imprint","INTERSECT",VERTEX,{"disambiguationData":[OD(0.0)],"derivedFrom":[subQ1,subQ0]});Q34=makeQuery(id+"F0.imprint","IMPRINT",FACE,{"disambiguationData":[TD([[makeQuery(id+"F0.imprint","IMPRINT",EDGE,{"disambiguationData":[TD([[subQ2,-1.0]])],"derivedFrom":subQ1}),-1.0]])]});}
            var Q35;
            {var subQ0=sQuery(id+"F0.wireOp",EDGE,"E4.16.1");var subQ1=sQuery(id+"F0.wireOp",EDGE,"E0");var subQ2=makeQuery(id+"F0.imprint","INTERSECT",VERTEX,{"disambiguationData":[OD(0.0)],"derivedFrom":[subQ1,subQ0]});Q35=makeQuery(id+"F0.imprint","IMPRINT",FACE,{"disambiguationData":[TD([[makeQuery(id+"F0.imprint","IMPRINT",EDGE,{"disambiguationData":[TD([[subQ2,-1.0]])],"derivedFrom":subQ1}),1.0]])]});}
            var Q36;
            {var subQ0=sQuery(id+"F0.wireOp",EDGE,"E4.14.1");var subQ1=sQuery(id+"F0.wireOp",EDGE,"E0");var subQ2=makeQuery(id+"F0.imprint","INTERSECT",VERTEX,{"disambiguationData":[OD(0.0)],"derivedFrom":[subQ1,subQ0]});Q36=makeQuery(id+"F0.imprint","IMPRINT",FACE,{"disambiguationData":[TD([[makeQuery(id+"F0.imprint","IMPRINT",EDGE,{"disambiguationData":[TD([[subQ2,-1.0]])],"derivedFrom":subQ1}),1.0]])]});}
            var Q37;
            {var subQ0=sQuery(id+"F0.wireOp",EDGE,"E4.13.1");var subQ1=sQuery(id+"F0.wireOp",EDGE,"E0");var subQ2=makeQuery(id+"F0.imprint","INTERSECT",VERTEX,{"disambiguationData":[OD(0.0)],"derivedFrom":[subQ1,subQ0]});Q37=makeQuery(id+"F0.imprint","IMPRINT",FACE,{"disambiguationData":[TD([[makeQuery(id+"F0.imprint","IMPRINT",EDGE,{"disambiguationData":[TD([[subQ2,-1.0]])],"derivedFrom":subQ1}),-1.0]])]});}
            var Q38;
            {var subQ0=sQuery(id+"F0.wireOp",EDGE,"E4.25.1");var subQ1=sQuery(id+"F0.wireOp",EDGE,"E0");var subQ2=makeQuery(id+"F0.imprint","INTERSECT",VERTEX,{"disambiguationData":[OD(0.0)],"derivedFrom":[subQ1,subQ0]});Q38=makeQuery(id+"F0.imprint","IMPRINT",FACE,{"disambiguationData":[TD([[makeQuery(id+"F0.imprint","IMPRINT",EDGE,{"disambiguationData":[TD([[subQ2,-1.0]])],"derivedFrom":subQ1}),-1.0]])]});}
            var Q39;
            {var subQ0=sQuery(id+"F0.wireOp",EDGE,"E4.32.1");var subQ1=sQuery(id+"F0.wireOp",EDGE,"E0");var subQ2=makeQuery(id+"F0.imprint","INTERSECT",VERTEX,{"disambiguationData":[OD(0.0)],"derivedFrom":[subQ1,subQ0]});Q39=makeQuery(id+"F0.imprint","IMPRINT",FACE,{"disambiguationData":[TD([[makeQuery(id+"F0.imprint","IMPRINT",EDGE,{"disambiguationData":[TD([[subQ2,-1.0]])],"derivedFrom":subQ1}),1.0]])]});}
            var Q40;
            {var subQ0=sQuery(id+"F0.wireOp",EDGE,"E4.24.1");var subQ1=sQuery(id+"F0.wireOp",EDGE,"E0");var subQ2=makeQuery(id+"F0.imprint","INTERSECT",VERTEX,{"disambiguationData":[OD(0.0)],"derivedFrom":[subQ1,subQ0]});Q40=makeQuery(id+"F0.imprint","IMPRINT",FACE,{"disambiguationData":[TD([[makeQuery(id+"F0.imprint","IMPRINT",EDGE,{"disambiguationData":[TD([[subQ2,-1.0]])],"derivedFrom":subQ1}),-1.0]])]});}
            var Q41;
            {var subQ0=sQuery(id+"F0.wireOp",EDGE,"E4.6.1");var subQ1=sQuery(id+"F0.wireOp",EDGE,"E0");var subQ2=makeQuery(id+"F0.imprint","INTERSECT",VERTEX,{"disambiguationData":[OD(0.0)],"derivedFrom":[subQ1,subQ0]});Q41=makeQuery(id+"F0.imprint","IMPRINT",FACE,{"disambiguationData":[TD([[makeQuery(id+"F0.imprint","IMPRINT",EDGE,{"disambiguationData":[TD([[subQ2,-1.0]])],"derivedFrom":subQ1}),-1.0]])]});}
            var Q42;
            {var subQ0=sQuery(id+"F0.wireOp",EDGE,"E4.11.1");var subQ1=sQuery(id+"F0.wireOp",EDGE,"E0");var subQ2=makeQuery(id+"F0.imprint","INTERSECT",VERTEX,{"disambiguationData":[OD(0.0)],"derivedFrom":[subQ1,subQ0]});Q42=makeQuery(id+"F0.imprint","IMPRINT",FACE,{"disambiguationData":[TD([[makeQuery(id+"F0.imprint","IMPRINT",EDGE,{"disambiguationData":[TD([[subQ2,-1.0]])],"derivedFrom":subQ1}),-1.0]])]});}
            var Q43;
            {var subQ0=sQuery(id+"F0.wireOp",EDGE,"E4.2.1");var subQ1=sQuery(id+"F0.wireOp",EDGE,"E0");var subQ2=makeQuery(id+"F0.imprint","INTERSECT",VERTEX,{"disambiguationData":[OD(0.0)],"derivedFrom":[subQ1,subQ0]});Q43=makeQuery(id+"F0.imprint","IMPRINT",FACE,{"disambiguationData":[TD([[makeQuery(id+"F0.imprint","IMPRINT",EDGE,{"disambiguationData":[TD([[subQ2,-1.0]])],"derivedFrom":subQ1}),-1.0]])]});}
            var Q44;
            {var subQ0=sQuery(id+"F0.wireOp",EDGE,"E4.23.1");var subQ1=sQuery(id+"F0.wireOp",EDGE,"E0");var subQ2=makeQuery(id+"F0.imprint","INTERSECT",VERTEX,{"disambiguationData":[OD(0.0)],"derivedFrom":[subQ1,subQ0]});Q44=makeQuery(id+"F0.imprint","IMPRINT",FACE,{"disambiguationData":[TD([[makeQuery(id+"F0.imprint","IMPRINT",EDGE,{"disambiguationData":[TD([[subQ2,-1.0]])],"derivedFrom":subQ1}),-1.0]])]});}
            var Q45;
            {var subQ0=sQuery(id+"F0.wireOp",EDGE,"E4.3.1");var subQ1=sQuery(id+"F0.wireOp",EDGE,"E0");var subQ2=makeQuery(id+"F0.imprint","INTERSECT",VERTEX,{"disambiguationData":[OD(0.0)],"derivedFrom":[subQ1,subQ0]});Q45=makeQuery(id+"F0.imprint","IMPRINT",FACE,{"disambiguationData":[TD([[makeQuery(id+"F0.imprint","IMPRINT",EDGE,{"disambiguationData":[TD([[subQ2,-1.0]])],"derivedFrom":subQ1}),1.0]])]});}
            var Q46;
            {var subQ0=sQuery(id+"F0.wireOp",EDGE,"E4.16.0");var subQ1=sQuery(id+"F0.wireOp",EDGE,"E0");var subQ2=makeQuery(id+"F0.imprint","INTERSECT",VERTEX,{"disambiguationData":[OD(1.0)],"derivedFrom":[subQ1,subQ0]});Q46=makeQuery(id+"F0.imprint","IMPRINT",FACE,{"disambiguationData":[TD([[makeQuery(id+"F0.imprint","IMPRINT",EDGE,{"disambiguationData":[TD([[subQ2,1.0]])],"derivedFrom":subQ1}),-1.0]])]});}
            var Q47;
            {var subQ0=sQuery(id+"F0.wireOp",EDGE,"E4.14.1");var subQ1=sQuery(id+"F0.wireOp",EDGE,"E0");var subQ2=makeQuery(id+"F0.imprint","INTERSECT",VERTEX,{"disambiguationData":[OD(0.0)],"derivedFrom":[subQ1,subQ0]});Q47=makeQuery(id+"F0.imprint","IMPRINT",FACE,{"disambiguationData":[TD([[makeQuery(id+"F0.imprint","IMPRINT",EDGE,{"disambiguationData":[TD([[subQ2,-1.0]])],"derivedFrom":subQ1}),-1.0]])]});}
            var Q48;
            {var subQ0=sQuery(id+"F0.wireOp",EDGE,"E4.5.1");var subQ1=sQuery(id+"F0.wireOp",EDGE,"E0");var subQ2=makeQuery(id+"F0.imprint","INTERSECT",VERTEX,{"disambiguationData":[OD(0.0)],"derivedFrom":[subQ1,subQ0]});Q48=makeQuery(id+"F0.imprint","IMPRINT",FACE,{"disambiguationData":[TD([[makeQuery(id+"F0.imprint","IMPRINT",EDGE,{"disambiguationData":[TD([[subQ2,-1.0]])],"derivedFrom":subQ1}),-1.0]])]});}
            var Q49;
            {var subQ0=sQuery(id+"F0.wireOp",EDGE,"E4.7.1");var subQ1=sQuery(id+"F0.wireOp",EDGE,"E0");var subQ2=makeQuery(id+"F0.imprint","INTERSECT",VERTEX,{"disambiguationData":[OD(0.0)],"derivedFrom":[subQ1,subQ0]});Q49=makeQuery(id+"F0.imprint","IMPRINT",FACE,{"disambiguationData":[TD([[makeQuery(id+"F0.imprint","IMPRINT",EDGE,{"disambiguationData":[TD([[subQ2,-1.0]])],"derivedFrom":subQ1}),1.0]])]});}
            var Q50;
            {var subQ0=sQuery(id+"F0.wireOp",EDGE,"E4.2.1");var subQ1=sQuery(id+"F0.wireOp",EDGE,"E0");var subQ2=makeQuery(id+"F0.imprint","INTERSECT",VERTEX,{"disambiguationData":[OD(0.0)],"derivedFrom":[subQ1,subQ0]});Q50=makeQuery(id+"F0.imprint","IMPRINT",FACE,{"disambiguationData":[TD([[makeQuery(id+"F0.imprint","IMPRINT",EDGE,{"disambiguationData":[TD([[subQ2,-1.0]])],"derivedFrom":subQ1}),1.0]])]});}
            var Q51;
            {var subQ0=sQuery(id+"F0.wireOp",EDGE,"E4.3.1");var subQ1=sQuery(id+"F0.wireOp",EDGE,"E0");var subQ2=makeQuery(id+"F0.imprint","INTERSECT",VERTEX,{"disambiguationData":[OD(0.0)],"derivedFrom":[subQ1,subQ0]});Q51=makeQuery(id+"F0.imprint","IMPRINT",FACE,{"disambiguationData":[TD([[makeQuery(id+"F0.imprint","IMPRINT",EDGE,{"disambiguationData":[TD([[subQ2,-1.0]])],"derivedFrom":subQ1}),-1.0]])]});}
            var Q52;
            {var subQ0=sQuery(id+"F0.wireOp",EDGE,"E4.11.1");var subQ1=sQuery(id+"F0.wireOp",EDGE,"E0");var subQ2=makeQuery(id+"F0.imprint","INTERSECT",VERTEX,{"disambiguationData":[OD(0.0)],"derivedFrom":[subQ1,subQ0]});Q52=makeQuery(id+"F0.imprint","IMPRINT",FACE,{"disambiguationData":[TD([[makeQuery(id+"F0.imprint","IMPRINT",EDGE,{"disambiguationData":[TD([[subQ2,-1.0]])],"derivedFrom":subQ1}),1.0]])]});}
            var Q53;
            {var subQ0=sQuery(id+"F0.wireOp",EDGE,"E4.17.1");var subQ1=sQuery(id+"F0.wireOp",EDGE,"E0");var subQ2=makeQuery(id+"F0.imprint","INTERSECT",VERTEX,{"disambiguationData":[OD(0.0)],"derivedFrom":[subQ1,subQ0]});Q53=makeQuery(id+"F0.imprint","IMPRINT",FACE,{"disambiguationData":[TD([[makeQuery(id+"F0.imprint","IMPRINT",EDGE,{"disambiguationData":[TD([[subQ2,-1.0]])],"derivedFrom":subQ1}),1.0]])]});}
            var Q54;
            {var subQ0=sQuery(id+"F0.wireOp",EDGE,"E4.15.0");var subQ1=sQuery(id+"F0.wireOp",EDGE,"E0");var subQ2=makeQuery(id+"F0.imprint","INTERSECT",VERTEX,{"disambiguationData":[OD(1.0)],"derivedFrom":[subQ1,subQ0]});Q54=makeQuery(id+"F0.imprint","IMPRINT",FACE,{"disambiguationData":[TD([[makeQuery(id+"F0.imprint","IMPRINT",EDGE,{"disambiguationData":[TD([[subQ2,1.0]])],"derivedFrom":subQ1}),-1.0]])]});}
            var Q55;
            {var subQ0=sQuery(id+"F0.wireOp",EDGE,"E4.25.2");var subQ1=sQuery(id+"F0.wireOp",EDGE,"E0");var subQ2=makeQuery(id+"F0.imprint","INTERSECT",VERTEX,{"derivedFrom":[subQ1,subQ0]});Q55=makeQuery(id+"F0.imprint","IMPRINT",FACE,{"disambiguationData":[TD([[makeQuery(id+"F0.imprint","IMPRINT",EDGE,{"disambiguationData":[TD([[subQ2,-1.0]])],"derivedFrom":subQ1}),-1.0]])]});}
            var Q56;
            {var subQ0=sQuery(id+"F0.wireOp",EDGE,"E4.29.1");var subQ1=sQuery(id+"F0.wireOp",EDGE,"E0");var subQ2=makeQuery(id+"F0.imprint","INTERSECT",VERTEX,{"disambiguationData":[OD(0.0)],"derivedFrom":[subQ1,subQ0]});Q56=makeQuery(id+"F0.imprint","IMPRINT",FACE,{"disambiguationData":[TD([[makeQuery(id+"F0.imprint","IMPRINT",EDGE,{"disambiguationData":[TD([[subQ2,-1.0]])],"derivedFrom":subQ1}),1.0]])]});}
            var Q57;
            {var subQ0=sQuery(id+"F0.wireOp",EDGE,"E4.29.1");var subQ1=sQuery(id+"F0.wireOp",EDGE,"E0");var subQ2=makeQuery(id+"F0.imprint","INTERSECT",VERTEX,{"disambiguationData":[OD(0.0)],"derivedFrom":[subQ1,subQ0]});Q57=makeQuery(id+"F0.imprint","IMPRINT",FACE,{"disambiguationData":[TD([[makeQuery(id+"F0.imprint","IMPRINT",EDGE,{"disambiguationData":[TD([[subQ2,-1.0]])],"derivedFrom":subQ1}),-1.0]])]});}
            var Q58;
            {var subQ0=sQuery(id+"F0.wireOp",EDGE,"E4.28.1");var subQ1=sQuery(id+"F0.wireOp",EDGE,"E0");var subQ2=makeQuery(id+"F0.imprint","INTERSECT",VERTEX,{"disambiguationData":[OD(0.0)],"derivedFrom":[subQ1,subQ0]});Q58=makeQuery(id+"F0.imprint","IMPRINT",FACE,{"disambiguationData":[TD([[makeQuery(id+"F0.imprint","IMPRINT",EDGE,{"disambiguationData":[TD([[subQ2,-1.0]])],"derivedFrom":subQ1}),-1.0]])]});}
            var Q59;
            {var subQ0=sQuery(id+"F0.wireOp",EDGE,"E4.22.1");var subQ1=sQuery(id+"F0.wireOp",EDGE,"E0");var subQ2=makeQuery(id+"F0.imprint","INTERSECT",VERTEX,{"disambiguationData":[OD(0.0)],"derivedFrom":[subQ1,subQ0]});Q59=makeQuery(id+"F0.imprint","IMPRINT",FACE,{"disambiguationData":[TD([[makeQuery(id+"F0.imprint","IMPRINT",EDGE,{"disambiguationData":[TD([[subQ2,-1.0]])],"derivedFrom":subQ1}),-1.0]])]});}
            var Q60;
            {var subQ0=sQuery(id+"F0.wireOp",EDGE,"E4.20.1");var subQ1=sQuery(id+"F0.wireOp",EDGE,"E0");var subQ2=makeQuery(id+"F0.imprint","INTERSECT",VERTEX,{"disambiguationData":[OD(0.0)],"derivedFrom":[subQ1,subQ0]});Q60=makeQuery(id+"F0.imprint","IMPRINT",FACE,{"disambiguationData":[TD([[makeQuery(id+"F0.imprint","IMPRINT",EDGE,{"disambiguationData":[TD([[subQ2,-1.0]])],"derivedFrom":subQ1}),-1.0]])]});}
            var Q61;
            {var subQ0=sQuery(id+"F0.wireOp",EDGE,"E4.34.1");var subQ1=sQuery(id+"F0.wireOp",EDGE,"E0");var subQ2=makeQuery(id+"F0.imprint","INTERSECT",VERTEX,{"disambiguationData":[OD(0.0)],"derivedFrom":[subQ1,subQ0]});Q61=makeQuery(id+"F0.imprint","IMPRINT",FACE,{"disambiguationData":[TD([[makeQuery(id+"F0.imprint","IMPRINT",EDGE,{"disambiguationData":[TD([[subQ2,-1.0]])],"derivedFrom":subQ1}),-1.0]])]});}
            var Q62;
            {var subQ0=sQuery(id+"F0.wireOp",EDGE,"E4.13.1");var subQ1=sQuery(id+"F0.wireOp",EDGE,"E0");var subQ2=makeQuery(id+"F0.imprint","INTERSECT",VERTEX,{"disambiguationData":[OD(0.0)],"derivedFrom":[subQ1,subQ0]});Q62=makeQuery(id+"F0.imprint","IMPRINT",FACE,{"disambiguationData":[TD([[makeQuery(id+"F0.imprint","IMPRINT",EDGE,{"disambiguationData":[TD([[subQ2,-1.0]])],"derivedFrom":subQ1}),1.0]])]});}
            var Q63;
            {var subQ0=sQuery(id+"F0.wireOp",EDGE,"E4.23.1");var subQ1=sQuery(id+"F0.wireOp",EDGE,"E0");var subQ2=makeQuery(id+"F0.imprint","INTERSECT",VERTEX,{"disambiguationData":[OD(0.0)],"derivedFrom":[subQ1,subQ0]});Q63=makeQuery(id+"F0.imprint","IMPRINT",FACE,{"disambiguationData":[TD([[makeQuery(id+"F0.imprint","IMPRINT",EDGE,{"disambiguationData":[TD([[subQ2,-1.0]])],"derivedFrom":subQ1}),1.0]])]});}
            var Q64;
            {var subQ0=sQuery(id+"F0.wireOp",EDGE,"E4.38.1");var subQ1=sQuery(id+"F0.wireOp",EDGE,"E0");var subQ2=makeQuery(id+"F0.imprint","INTERSECT",VERTEX,{"disambiguationData":[OD(0.0)],"derivedFrom":[subQ1,subQ0]});Q64=makeQuery(id+"F0.imprint","IMPRINT",FACE,{"disambiguationData":[TD([[makeQuery(id+"F0.imprint","IMPRINT",EDGE,{"disambiguationData":[TD([[subQ2,-1.0]])],"derivedFrom":subQ1}),-1.0]])]});}
            var Q65;
            {var subQ0=sQuery(id+"F0.wireOp",EDGE,"E4.9.1");var subQ1=sQuery(id+"F0.wireOp",EDGE,"E0");var subQ2=makeQuery(id+"F0.imprint","INTERSECT",VERTEX,{"disambiguationData":[OD(0.0)],"derivedFrom":[subQ1,subQ0]});Q65=makeQuery(id+"F0.imprint","IMPRINT",FACE,{"disambiguationData":[TD([[makeQuery(id+"F0.imprint","IMPRINT",EDGE,{"disambiguationData":[TD([[subQ2,-1.0]])],"derivedFrom":subQ1}),1.0]])]});}
            var Q66;
            {var subQ0=sQuery(id+"F0.wireOp",EDGE,"E4.8.1");var subQ1=sQuery(id+"F0.wireOp",EDGE,"E0");var subQ2=makeQuery(id+"F0.imprint","INTERSECT",VERTEX,{"disambiguationData":[OD(0.0)],"derivedFrom":[subQ1,subQ0]});Q66=makeQuery(id+"F0.imprint","IMPRINT",FACE,{"disambiguationData":[TD([[makeQuery(id+"F0.imprint","IMPRINT",EDGE,{"disambiguationData":[TD([[subQ2,-1.0]])],"derivedFrom":subQ1}),1.0]])]});}
            var Q67;
            {var subQ0=sQuery(id+"F0.wireOp",EDGE,"E4.31.1");var subQ1=sQuery(id+"F0.wireOp",EDGE,"E0");var subQ2=makeQuery(id+"F0.imprint","INTERSECT",VERTEX,{"disambiguationData":[OD(0.0)],"derivedFrom":[subQ1,subQ0]});Q67=makeQuery(id+"F0.imprint","IMPRINT",FACE,{"disambiguationData":[TD([[makeQuery(id+"F0.imprint","IMPRINT",EDGE,{"disambiguationData":[TD([[subQ2,-1.0]])],"derivedFrom":subQ1}),1.0]])]});}
            var Q68;
            {var subQ0=sQuery(id+"F0.wireOp",EDGE,"E4.35.1");var subQ1=sQuery(id+"F0.wireOp",EDGE,"E0");var subQ2=makeQuery(id+"F0.imprint","INTERSECT",VERTEX,{"disambiguationData":[OD(0.0)],"derivedFrom":[subQ1,subQ0]});Q68=makeQuery(id+"F0.imprint","IMPRINT",FACE,{"disambiguationData":[TD([[makeQuery(id+"F0.imprint","IMPRINT",EDGE,{"disambiguationData":[TD([[subQ2,-1.0]])],"derivedFrom":subQ1}),-1.0]])]});}
            var Q69;
            {var subQ0=sQuery(id+"F0.wireOp",EDGE,"E4.17.1");var subQ1=sQuery(id+"F0.wireOp",EDGE,"E0");var subQ2=makeQuery(id+"F0.imprint","INTERSECT",VERTEX,{"disambiguationData":[OD(0.0)],"derivedFrom":[subQ1,subQ0]});Q69=makeQuery(id+"F0.imprint","IMPRINT",FACE,{"disambiguationData":[TD([[makeQuery(id+"F0.imprint","IMPRINT",EDGE,{"disambiguationData":[TD([[subQ2,-1.0]])],"derivedFrom":subQ1}),-1.0]])]});}
            var Q70;
            {var subQ0=sQuery(id+"F0.wireOp",EDGE,"E4.16.1");var subQ1=sQuery(id+"F0.wireOp",EDGE,"E0");var subQ2=makeQuery(id+"F0.imprint","INTERSECT",VERTEX,{"disambiguationData":[OD(0.0)],"derivedFrom":[subQ1,subQ0]});Q70=makeQuery(id+"F0.imprint","IMPRINT",FACE,{"disambiguationData":[TD([[makeQuery(id+"F0.imprint","IMPRINT",EDGE,{"disambiguationData":[TD([[subQ2,-1.0]])],"derivedFrom":subQ1}),-1.0]])]});}
            var Q71;
            {var subQ0=sQuery(id+"F0.wireOp",EDGE,"E4.15.1");var subQ1=sQuery(id+"F0.wireOp",EDGE,"E0");var subQ2=makeQuery(id+"F0.imprint","INTERSECT",VERTEX,{"disambiguationData":[OD(0.0)],"derivedFrom":[subQ1,subQ0]});Q71=makeQuery(id+"F0.imprint","IMPRINT",FACE,{"disambiguationData":[TD([[makeQuery(id+"F0.imprint","IMPRINT",EDGE,{"disambiguationData":[TD([[subQ2,-1.0]])],"derivedFrom":subQ1}),1.0]])]});}
            var Q72;
            {var subQ0=sQuery(id+"F0.wireOp",EDGE,"E4.28.1");var subQ1=sQuery(id+"F0.wireOp",EDGE,"E0");var subQ2=makeQuery(id+"F0.imprint","INTERSECT",VERTEX,{"disambiguationData":[OD(0.0)],"derivedFrom":[subQ1,subQ0]});Q72=makeQuery(id+"F0.imprint","IMPRINT",FACE,{"disambiguationData":[TD([[makeQuery(id+"F0.imprint","IMPRINT",EDGE,{"disambiguationData":[TD([[subQ2,-1.0]])],"derivedFrom":subQ1}),1.0]])]});}
            var Q73;
            {var subQ0=sQuery(id+"F0.wireOp",EDGE,"E4.5.1");var subQ1=sQuery(id+"F0.wireOp",EDGE,"E0");var subQ2=makeQuery(id+"F0.imprint","INTERSECT",VERTEX,{"disambiguationData":[OD(0.0)],"derivedFrom":[subQ1,subQ0]});Q73=makeQuery(id+"F0.imprint","IMPRINT",FACE,{"disambiguationData":[TD([[makeQuery(id+"F0.imprint","IMPRINT",EDGE,{"disambiguationData":[TD([[subQ2,-1.0]])],"derivedFrom":subQ1}),1.0]])]});}
            var Q74;
            {var subQ0=sQuery(id+"F0.wireOp",EDGE,"E4.1.2");var subQ1=sQuery(id+"F0.wireOp",EDGE,"E0");var subQ2=makeQuery(id+"F0.imprint","INTERSECT",VERTEX,{"derivedFrom":[subQ1,subQ0]});Q74=makeQuery(id+"F0.imprint","IMPRINT",FACE,{"disambiguationData":[TD([[makeQuery(id+"F0.imprint","IMPRINT",EDGE,{"disambiguationData":[TD([[subQ2,-1.0]])],"derivedFrom":subQ1}),-1.0]])]});}
            var Q75;
            {var subQ0=sQuery(id+"F0.wireOp",EDGE,"E4.4.1");var subQ1=sQuery(id+"F0.wireOp",EDGE,"E0");var subQ2=makeQuery(id+"F0.imprint","INTERSECT",VERTEX,{"disambiguationData":[OD(0.0)],"derivedFrom":[subQ1,subQ0]});Q75=makeQuery(id+"F0.imprint","IMPRINT",FACE,{"disambiguationData":[TD([[makeQuery(id+"F0.imprint","IMPRINT",EDGE,{"disambiguationData":[TD([[subQ2,-1.0]])],"derivedFrom":subQ1}),-1.0]])]});}
            var Q76;
            {var subQ0=sQuery(id+"F0.wireOp",EDGE,"E4.12.1");var subQ1=sQuery(id+"F0.wireOp",EDGE,"E0");var subQ2=makeQuery(id+"F0.imprint","INTERSECT",VERTEX,{"disambiguationData":[OD(0.0)],"derivedFrom":[subQ1,subQ0]});Q76=makeQuery(id+"F0.imprint","IMPRINT",FACE,{"disambiguationData":[TD([[makeQuery(id+"F0.imprint","IMPRINT",EDGE,{"disambiguationData":[TD([[subQ2,-1.0]])],"derivedFrom":subQ1}),1.0]])]});}
            var Q77;
            {var subQ0=sQuery(id+"F0.wireOp",EDGE,"E4.1.1");var subQ1=sQuery(id+"F0.wireOp",EDGE,"E0");var subQ2=makeQuery(id+"F0.imprint","INTERSECT",VERTEX,{"disambiguationData":[OD(0.0)],"derivedFrom":[subQ1,subQ0]});Q77=makeQuery(id+"F0.imprint","IMPRINT",FACE,{"disambiguationData":[TD([[makeQuery(id+"F0.imprint","IMPRINT",EDGE,{"disambiguationData":[TD([[subQ2,-1.0]])],"derivedFrom":subQ1}),1.0]])]});}
            var Q78;
            {var subQ0=sQuery(id+"F0.wireOp",EDGE,"E4.25.1");var subQ1=sQuery(id+"F0.wireOp",EDGE,"E0");var subQ2=makeQuery(id+"F0.imprint","INTERSECT",VERTEX,{"disambiguationData":[OD(0.0)],"derivedFrom":[subQ1,subQ0]});Q78=makeQuery(id+"F0.imprint","IMPRINT",FACE,{"disambiguationData":[TD([[makeQuery(id+"F0.imprint","IMPRINT",EDGE,{"disambiguationData":[TD([[subQ2,-1.0]])],"derivedFrom":subQ1}),1.0]])]});}
            var Q79;
            {var subQ0=sQuery(id+"F0.wireOp",EDGE,"E4.39.1");var subQ1=sQuery(id+"F0.wireOp",EDGE,"E0");var subQ2=makeQuery(id+"F0.imprint","INTERSECT",VERTEX,{"disambiguationData":[OD(0.0)],"derivedFrom":[subQ1,subQ0]});Q79=makeQuery(id+"F0.imprint","IMPRINT",FACE,{"disambiguationData":[TD([[makeQuery(id+"F0.imprint","IMPRINT",EDGE,{"disambiguationData":[TD([[subQ2,-1.0]])],"derivedFrom":subQ1}),-1.0]])]});}
            var Q80;
            {var subQ0=sQuery(id+"F0.wireOp",EDGE,"E4.27.1");var subQ1=sQuery(id+"F0.wireOp",EDGE,"E0");var subQ2=makeQuery(id+"F0.imprint","INTERSECT",VERTEX,{"disambiguationData":[OD(0.0)],"derivedFrom":[subQ1,subQ0]});Q80=makeQuery(id+"F0.imprint","IMPRINT",FACE,{"disambiguationData":[TD([[makeQuery(id+"F0.imprint","IMPRINT",EDGE,{"disambiguationData":[TD([[subQ2,-1.0]])],"derivedFrom":subQ1}),-1.0]])]});}
            var Q81;
            {var subQ0=sQuery(id+"F0.wireOp",EDGE,"E4.8.1");var subQ1=sQuery(id+"F0.wireOp",EDGE,"E0");var subQ2=makeQuery(id+"F0.imprint","INTERSECT",VERTEX,{"disambiguationData":[OD(0.0)],"derivedFrom":[subQ1,subQ0]});Q81=makeQuery(id+"F0.imprint","IMPRINT",FACE,{"disambiguationData":[TD([[makeQuery(id+"F0.imprint","IMPRINT",EDGE,{"disambiguationData":[TD([[subQ2,-1.0]])],"derivedFrom":subQ1}),-1.0]])]});}
            var Q82;
            {var subQ0=sQuery(id+"F0.wireOp",EDGE,"E4.39.0");var subQ1=sQuery(id+"F0.wireOp",EDGE,"E0");var subQ2=makeQuery(id+"F0.imprint","INTERSECT",VERTEX,{"disambiguationData":[OD(1.0)],"derivedFrom":[subQ1,subQ0]});Q82=makeQuery(id+"F0.imprint","IMPRINT",FACE,{"disambiguationData":[TD([[makeQuery(id+"F0.imprint","IMPRINT",EDGE,{"disambiguationData":[TD([[subQ2,1.0]])],"derivedFrom":subQ1}),-1.0]])]});}
            var Q83;
            {var subQ0=sQuery(id+"F0.wireOp",EDGE,"E4.38.1");var subQ1=sQuery(id+"F0.wireOp",EDGE,"E0");var subQ2=makeQuery(id+"F0.imprint","INTERSECT",VERTEX,{"disambiguationData":[OD(0.0)],"derivedFrom":[subQ1,subQ0]});Q83=makeQuery(id+"F0.imprint","IMPRINT",FACE,{"disambiguationData":[TD([[makeQuery(id+"F0.imprint","IMPRINT",EDGE,{"disambiguationData":[TD([[subQ2,-1.0]])],"derivedFrom":subQ1}),1.0]])]});}
            var Q84;
            {var subQ0=sQuery(id+"F0.wireOp",EDGE,"E1");var subQ1=sQuery(id+"F0.wireOp",EDGE,"E0");var subQ2=makeQuery(id+"F0.imprint","INTERSECT",VERTEX,{"disambiguationData":[OD(0.0)],"derivedFrom":[subQ1,subQ0]});Q84=makeQuery(id+"F0.imprint","IMPRINT",FACE,{"disambiguationData":[TD([[makeQuery(id+"F0.imprint","IMPRINT",EDGE,{"disambiguationData":[TD([[subQ2,-1.0]])],"derivedFrom":subQ1}),-1.0]])]});}
            var Q85;
            {var subQ0=sQuery(id+"F0.wireOp",EDGE,"E4.24.1");var subQ1=sQuery(id+"F0.wireOp",EDGE,"E0");var subQ2=makeQuery(id+"F0.imprint","INTERSECT",VERTEX,{"disambiguationData":[OD(0.0)],"derivedFrom":[subQ1,subQ0]});Q85=makeQuery(id+"F0.imprint","IMPRINT",FACE,{"disambiguationData":[TD([[makeQuery(id+"F0.imprint","IMPRINT",EDGE,{"disambiguationData":[TD([[subQ2,-1.0]])],"derivedFrom":subQ1}),1.0]])]});}
            var Q86;
            {var subQ0=sQuery(id+"F0.wireOp",EDGE,"E4.35.1");var subQ1=sQuery(id+"F0.wireOp",EDGE,"E0");var subQ2=makeQuery(id+"F0.imprint","INTERSECT",VERTEX,{"disambiguationData":[OD(0.0)],"derivedFrom":[subQ1,subQ0]});Q86=makeQuery(id+"F0.imprint","IMPRINT",FACE,{"disambiguationData":[TD([[makeQuery(id+"F0.imprint","IMPRINT",EDGE,{"disambiguationData":[TD([[subQ2,-1.0]])],"derivedFrom":subQ1}),1.0]])]});}
            var Q87;
            {var subQ0=sQuery(id+"F0.wireOp",EDGE,"E4.30.1");var subQ1=sQuery(id+"F0.wireOp",EDGE,"E0");var subQ2=makeQuery(id+"F0.imprint","INTERSECT",VERTEX,{"disambiguationData":[OD(0.0)],"derivedFrom":[subQ1,subQ0]});Q87=makeQuery(id+"F0.imprint","IMPRINT",FACE,{"disambiguationData":[TD([[makeQuery(id+"F0.imprint","IMPRINT",EDGE,{"disambiguationData":[TD([[subQ2,1.0]])],"derivedFrom":subQ1}),-1.0]])]});}
            var Q88;
            {var subQ0=sQuery(id+"F0.wireOp",EDGE,"E4.22.1");var subQ1=sQuery(id+"F0.wireOp",EDGE,"E0");var subQ2=makeQuery(id+"F0.imprint","INTERSECT",VERTEX,{"disambiguationData":[OD(0.0)],"derivedFrom":[subQ1,subQ0]});Q88=makeQuery(id+"F0.imprint","IMPRINT",FACE,{"disambiguationData":[TD([[makeQuery(id+"F0.imprint","IMPRINT",EDGE,{"disambiguationData":[TD([[subQ2,-1.0]])],"derivedFrom":subQ1}),1.0]])]});}
            var Q89;
            {var subQ0=sQuery(id+"F0.wireOp",EDGE,"E3");var subQ1=sQuery(id+"F0.wireOp",EDGE,"E0");var subQ2=makeQuery(id+"F0.imprint","INTERSECT",VERTEX,{"derivedFrom":[subQ1,subQ0]});Q89=makeQuery(id+"F0.imprint","IMPRINT",FACE,{"disambiguationData":[TD([[makeQuery(id+"F0.imprint","IMPRINT",EDGE,{"disambiguationData":[TD([[subQ2,-1.0]])],"derivedFrom":subQ1}),-1.0]])]});}
            var Q90;
            {var subQ0=sQuery(id+"F0.wireOp",EDGE,"E4.24.0");var subQ1=sQuery(id+"F0.wireOp",EDGE,"E0");var subQ2=makeQuery(id+"F0.imprint","INTERSECT",VERTEX,{"disambiguationData":[OD(1.0)],"derivedFrom":[subQ1,subQ0]});Q90=makeQuery(id+"F0.imprint","IMPRINT",FACE,{"disambiguationData":[TD([[makeQuery(id+"F0.imprint","IMPRINT",EDGE,{"disambiguationData":[TD([[subQ2,1.0]])],"derivedFrom":subQ1}),-1.0]])]});}
            var Q91;
            {var subQ0=sQuery(id+"F0.wireOp",EDGE,"E4.27.0");var subQ1=sQuery(id+"F0.wireOp",EDGE,"E0");var subQ2=makeQuery(id+"F0.imprint","INTERSECT",VERTEX,{"disambiguationData":[OD(1.0)],"derivedFrom":[subQ1,subQ0]});Q91=makeQuery(id+"F0.imprint","IMPRINT",FACE,{"disambiguationData":[TD([[makeQuery(id+"F0.imprint","IMPRINT",EDGE,{"disambiguationData":[TD([[subQ2,1.0]])],"derivedFrom":subQ1}),-1.0]])]});}
            var Q92;
            {var subQ0=sQuery(id+"F0.wireOp",EDGE,"E4.21.0");var subQ1=sQuery(id+"F0.wireOp",EDGE,"E0");var subQ2=makeQuery(id+"F0.imprint","INTERSECT",VERTEX,{"disambiguationData":[OD(1.0)],"derivedFrom":[subQ1,subQ0]});Q92=makeQuery(id+"F0.imprint","IMPRINT",FACE,{"disambiguationData":[TD([[makeQuery(id+"F0.imprint","IMPRINT",EDGE,{"disambiguationData":[TD([[subQ2,1.0]])],"derivedFrom":subQ1}),-1.0]])]});}
            var Q93;
            {var subQ0=sQuery(id+"F0.wireOp",EDGE,"E4.2.2");var subQ1=sQuery(id+"F0.wireOp",EDGE,"E0");var subQ2=makeQuery(id+"F0.imprint","INTERSECT",VERTEX,{"derivedFrom":[subQ1,subQ0]});Q93=makeQuery(id+"F0.imprint","IMPRINT",FACE,{"disambiguationData":[TD([[makeQuery(id+"F0.imprint","IMPRINT",EDGE,{"disambiguationData":[TD([[subQ2,-1.0]])],"derivedFrom":subQ1}),-1.0]])]});}
            var Q94;
            {var subQ0=sQuery(id+"F0.wireOp",EDGE,"E2");var subQ1=sQuery(id+"F0.wireOp",EDGE,"E0");var subQ2=makeQuery(id+"F0.imprint","INTERSECT",VERTEX,{"disambiguationData":[OD(0.0)],"derivedFrom":[subQ1,subQ0]});Q94=makeQuery(id+"F0.imprint","IMPRINT",FACE,{"disambiguationData":[TD([[makeQuery(id+"F0.imprint","IMPRINT",EDGE,{"disambiguationData":[TD([[subQ2,1.0]])],"derivedFrom":subQ1}),1.0]])]});}
            var Q95;
            {var subQ0=sQuery(id+"F0.wireOp",EDGE,"E4.38.2");var subQ1=sQuery(id+"F0.wireOp",EDGE,"E0");var subQ2=makeQuery(id+"F0.imprint","INTERSECT",VERTEX,{"derivedFrom":[subQ1,subQ0]});Q95=makeQuery(id+"F0.imprint","IMPRINT",FACE,{"disambiguationData":[TD([[makeQuery(id+"F0.imprint","IMPRINT",EDGE,{"disambiguationData":[TD([[subQ2,-1.0]])],"derivedFrom":subQ1}),-1.0]])]});}
            var Q96;
            {var subQ0=sQuery(id+"F0.wireOp",EDGE,"E4.20.0");var subQ1=sQuery(id+"F0.wireOp",EDGE,"E0");var subQ2=makeQuery(id+"F0.imprint","INTERSECT",VERTEX,{"disambiguationData":[OD(0.0)],"derivedFrom":[subQ1,subQ0]});Q96=makeQuery(id+"F0.imprint","IMPRINT",FACE,{"disambiguationData":[TD([[makeQuery(id+"F0.imprint","IMPRINT",EDGE,{"disambiguationData":[TD([[subQ2,1.0]])],"derivedFrom":subQ1}),1.0]])]});}
            var Q97;
            {var subQ0=sQuery(id+"F0.wireOp",EDGE,"E4.32.0");var subQ1=sQuery(id+"F0.wireOp",EDGE,"E0");var subQ2=makeQuery(id+"F0.imprint","INTERSECT",VERTEX,{"disambiguationData":[OD(1.0)],"derivedFrom":[subQ1,subQ0]});Q97=makeQuery(id+"F0.imprint","IMPRINT",FACE,{"disambiguationData":[TD([[makeQuery(id+"F0.imprint","IMPRINT",EDGE,{"disambiguationData":[TD([[subQ2,1.0]])],"derivedFrom":subQ1}),-1.0]])]});}
            var Q98;
            {var subQ0=sQuery(id+"F0.wireOp",EDGE,"E4.28.0");var subQ1=sQuery(id+"F0.wireOp",EDGE,"E0");var subQ2=makeQuery(id+"F0.imprint","INTERSECT",VERTEX,{"disambiguationData":[OD(1.0)],"derivedFrom":[subQ1,subQ0]});Q98=makeQuery(id+"F0.imprint","IMPRINT",FACE,{"disambiguationData":[TD([[makeQuery(id+"F0.imprint","IMPRINT",EDGE,{"disambiguationData":[TD([[subQ2,1.0]])],"derivedFrom":subQ1}),-1.0]])]});}
            var Q99;
            {var subQ0=sQuery(id+"F0.wireOp",EDGE,"E4.19.0");var subQ1=sQuery(id+"F0.wireOp",EDGE,"E0");var subQ2=makeQuery(id+"F0.imprint","INTERSECT",VERTEX,{"disambiguationData":[OD(0.0)],"derivedFrom":[subQ1,subQ0]});Q99=makeQuery(id+"F0.imprint","IMPRINT",FACE,{"disambiguationData":[TD([[makeQuery(id+"F0.imprint","IMPRINT",EDGE,{"disambiguationData":[TD([[subQ2,1.0]])],"derivedFrom":subQ1}),1.0]])]});}
            var Q100;
            {var subQ0=sQuery(id+"F0.wireOp",EDGE,"E4.37.0");var subQ1=sQuery(id+"F0.wireOp",EDGE,"E0");var subQ2=makeQuery(id+"F0.imprint","INTERSECT",VERTEX,{"disambiguationData":[OD(0.0)],"derivedFrom":[subQ1,subQ0]});Q100=makeQuery(id+"F0.imprint","IMPRINT",FACE,{"disambiguationData":[TD([[makeQuery(id+"F0.imprint","IMPRINT",EDGE,{"disambiguationData":[TD([[subQ2,1.0]])],"derivedFrom":subQ1}),1.0]])]});}
            var Q101;
            {var subQ0=sQuery(id+"F0.wireOp",EDGE,"E4.12.0");var subQ1=sQuery(id+"F0.wireOp",EDGE,"E0");var subQ2=makeQuery(id+"F0.imprint","INTERSECT",VERTEX,{"disambiguationData":[OD(1.0)],"derivedFrom":[subQ1,subQ0]});Q101=makeQuery(id+"F0.imprint","IMPRINT",FACE,{"disambiguationData":[TD([[makeQuery(id+"F0.imprint","IMPRINT",EDGE,{"disambiguationData":[TD([[subQ2,1.0]])],"derivedFrom":subQ1}),-1.0]])]});}
            var Q102;
            {var subQ0=sQuery(id+"F0.wireOp",EDGE,"E4.35.2");var subQ1=sQuery(id+"F0.wireOp",EDGE,"E0");var subQ2=makeQuery(id+"F0.imprint","INTERSECT",VERTEX,{"derivedFrom":[subQ1,subQ0]});Q102=makeQuery(id+"F0.imprint","IMPRINT",FACE,{"disambiguationData":[TD([[makeQuery(id+"F0.imprint","IMPRINT",EDGE,{"disambiguationData":[TD([[subQ2,-1.0]])],"derivedFrom":subQ1}),-1.0]])]});}
            var Q103;
            {var subQ0=sQuery(id+"F0.wireOp",EDGE,"E4.12.2");var subQ1=sQuery(id+"F0.wireOp",EDGE,"E0");var subQ2=makeQuery(id+"F0.imprint","INTERSECT",VERTEX,{"derivedFrom":[subQ1,subQ0]});Q103=makeQuery(id+"F0.imprint","IMPRINT",FACE,{"disambiguationData":[TD([[makeQuery(id+"F0.imprint","IMPRINT",EDGE,{"disambiguationData":[TD([[subQ2,-1.0]])],"derivedFrom":subQ1}),-1.0]])]});}
            var Q104;
            {var subQ0=sQuery(id+"F0.wireOp",EDGE,"E4.4.0");var subQ1=sQuery(id+"F0.wireOp",EDGE,"E0");var subQ2=makeQuery(id+"F0.imprint","INTERSECT",VERTEX,{"disambiguationData":[OD(0.0)],"derivedFrom":[subQ1,subQ0]});Q104=makeQuery(id+"F0.imprint","IMPRINT",FACE,{"disambiguationData":[TD([[makeQuery(id+"F0.imprint","IMPRINT",EDGE,{"disambiguationData":[TD([[subQ2,1.0]])],"derivedFrom":subQ1}),1.0]])]});}
            var Q105;
            {var subQ0=sQuery(id+"F0.wireOp",EDGE,"E4.9.0");var subQ1=sQuery(id+"F0.wireOp",EDGE,"E0");var subQ2=makeQuery(id+"F0.imprint","INTERSECT",VERTEX,{"disambiguationData":[OD(0.0)],"derivedFrom":[subQ1,subQ0]});Q105=makeQuery(id+"F0.imprint","IMPRINT",FACE,{"disambiguationData":[TD([[makeQuery(id+"F0.imprint","IMPRINT",EDGE,{"disambiguationData":[TD([[subQ2,1.0]])],"derivedFrom":subQ1}),1.0]])]});}
            var Q106;
            {var subQ0=sQuery(id+"F0.wireOp",EDGE,"E4.36.0");var subQ1=sQuery(id+"F0.wireOp",EDGE,"E0");var subQ2=makeQuery(id+"F0.imprint","INTERSECT",VERTEX,{"disambiguationData":[OD(0.0)],"derivedFrom":[subQ1,subQ0]});Q106=makeQuery(id+"F0.imprint","IMPRINT",FACE,{"disambiguationData":[TD([[makeQuery(id+"F0.imprint","IMPRINT",EDGE,{"disambiguationData":[TD([[subQ2,1.0]])],"derivedFrom":subQ1}),1.0]])]});}
            var Q107;
            {var subQ0=sQuery(id+"F0.wireOp",EDGE,"E4.18.0");var subQ1=sQuery(id+"F0.wireOp",EDGE,"E0");var subQ2=makeQuery(id+"F0.imprint","INTERSECT",VERTEX,{"disambiguationData":[OD(1.0)],"derivedFrom":[subQ1,subQ0]});Q107=makeQuery(id+"F0.imprint","IMPRINT",FACE,{"disambiguationData":[TD([[makeQuery(id+"F0.imprint","IMPRINT",EDGE,{"disambiguationData":[TD([[subQ2,1.0]])],"derivedFrom":subQ1}),-1.0]])]});}
            var Q108;
            {var subQ0=sQuery(id+"F0.wireOp",EDGE,"E4.23.2");var subQ1=sQuery(id+"F0.wireOp",EDGE,"E0");var subQ2=makeQuery(id+"F0.imprint","INTERSECT",VERTEX,{"derivedFrom":[subQ1,subQ0]});Q108=makeQuery(id+"F0.imprint","IMPRINT",FACE,{"disambiguationData":[TD([[makeQuery(id+"F0.imprint","IMPRINT",EDGE,{"disambiguationData":[TD([[subQ2,-1.0]])],"derivedFrom":subQ1}),-1.0]])]});}
            var Q109;
            {var subQ0=sQuery(id+"F0.wireOp",EDGE,"E4.6.0");var subQ1=sQuery(id+"F0.wireOp",EDGE,"E0");var subQ2=makeQuery(id+"F0.imprint","INTERSECT",VERTEX,{"disambiguationData":[OD(0.0)],"derivedFrom":[subQ1,subQ0]});Q109=makeQuery(id+"F0.imprint","IMPRINT",FACE,{"disambiguationData":[TD([[makeQuery(id+"F0.imprint","IMPRINT",EDGE,{"disambiguationData":[TD([[subQ2,1.0]])],"derivedFrom":subQ1}),1.0]])]});}
            var Q110;
            {var subQ0=sQuery(id+"F0.wireOp",EDGE,"E4.3.2");var subQ1=sQuery(id+"F0.wireOp",EDGE,"E0");var subQ2=makeQuery(id+"F0.imprint","INTERSECT",VERTEX,{"derivedFrom":[subQ1,subQ0]});Q110=makeQuery(id+"F0.imprint","IMPRINT",FACE,{"disambiguationData":[TD([[makeQuery(id+"F0.imprint","IMPRINT",EDGE,{"disambiguationData":[TD([[subQ2,-1.0]])],"derivedFrom":subQ1}),-1.0]])]});}
            var Q111;
            {var subQ0=sQuery(id+"F0.wireOp",EDGE,"E4.32.2");var subQ1=sQuery(id+"F0.wireOp",EDGE,"E0");var subQ2=makeQuery(id+"F0.imprint","INTERSECT",VERTEX,{"derivedFrom":[subQ1,subQ0]});Q111=makeQuery(id+"F0.imprint","IMPRINT",FACE,{"disambiguationData":[TD([[makeQuery(id+"F0.imprint","IMPRINT",EDGE,{"disambiguationData":[TD([[subQ2,-1.0]])],"derivedFrom":subQ1}),-1.0]])]});}
            var Q112;
            {var subQ0=sQuery(id+"F0.wireOp",EDGE,"E4.34.0");var subQ1=sQuery(id+"F0.wireOp",EDGE,"E0");var subQ2=makeQuery(id+"F0.imprint","INTERSECT",VERTEX,{"disambiguationData":[OD(0.0)],"derivedFrom":[subQ1,subQ0]});Q112=makeQuery(id+"F0.imprint","IMPRINT",FACE,{"disambiguationData":[TD([[makeQuery(id+"F0.imprint","IMPRINT",EDGE,{"disambiguationData":[TD([[subQ2,1.0]])],"derivedFrom":subQ1}),1.0]])]});}
            var Q113;
            {var subQ0=sQuery(id+"F0.wireOp",EDGE,"E4.22.2");var subQ1=sQuery(id+"F0.wireOp",EDGE,"E0");var subQ2=makeQuery(id+"F0.imprint","INTERSECT",VERTEX,{"derivedFrom":[subQ1,subQ0]});Q113=makeQuery(id+"F0.imprint","IMPRINT",FACE,{"disambiguationData":[TD([[makeQuery(id+"F0.imprint","IMPRINT",EDGE,{"disambiguationData":[TD([[subQ2,-1.0]])],"derivedFrom":subQ1}),-1.0]])]});}
            var Q114;
            {var subQ0=sQuery(id+"F0.wireOp",EDGE,"E4.26.0");var subQ1=sQuery(id+"F0.wireOp",EDGE,"E0");var subQ2=makeQuery(id+"F0.imprint","INTERSECT",VERTEX,{"disambiguationData":[OD(0.0)],"derivedFrom":[subQ1,subQ0]});Q114=makeQuery(id+"F0.imprint","IMPRINT",FACE,{"disambiguationData":[TD([[makeQuery(id+"F0.imprint","IMPRINT",EDGE,{"disambiguationData":[TD([[subQ2,1.0]])],"derivedFrom":subQ1}),1.0]])]});}
            var Q115;
            {var subQ0=sQuery(id+"F0.wireOp",EDGE,"E4.24.0");var subQ1=sQuery(id+"F0.wireOp",EDGE,"E0");var subQ2=makeQuery(id+"F0.imprint","INTERSECT",VERTEX,{"disambiguationData":[OD(0.0)],"derivedFrom":[subQ1,subQ0]});Q115=makeQuery(id+"F0.imprint","IMPRINT",FACE,{"disambiguationData":[TD([[makeQuery(id+"F0.imprint","IMPRINT",EDGE,{"disambiguationData":[TD([[subQ2,1.0]])],"derivedFrom":subQ1}),1.0]])]});}
            var Q116;
            {var subQ0=sQuery(id+"F0.wireOp",EDGE,"E4.15.0");var subQ1=sQuery(id+"F0.wireOp",EDGE,"E0");var subQ2=makeQuery(id+"F0.imprint","INTERSECT",VERTEX,{"disambiguationData":[OD(0.0)],"derivedFrom":[subQ1,subQ0]});Q116=makeQuery(id+"F0.imprint","IMPRINT",FACE,{"disambiguationData":[TD([[makeQuery(id+"F0.imprint","IMPRINT",EDGE,{"disambiguationData":[TD([[subQ2,1.0]])],"derivedFrom":subQ1}),1.0]])]});}
            var Q117;
            {var subQ0=sQuery(id+"F0.wireOp",EDGE,"E4.36.0");var subQ1=sQuery(id+"F0.wireOp",EDGE,"E0");var subQ2=makeQuery(id+"F0.imprint","INTERSECT",VERTEX,{"disambiguationData":[OD(1.0)],"derivedFrom":[subQ1,subQ0]});Q117=makeQuery(id+"F0.imprint","IMPRINT",FACE,{"disambiguationData":[TD([[makeQuery(id+"F0.imprint","IMPRINT",EDGE,{"disambiguationData":[TD([[subQ2,1.0]])],"derivedFrom":subQ1}),-1.0]])]});}
            var Q118;
            {var subQ0=sQuery(id+"F0.wireOp",EDGE,"E4.21.2");var subQ1=sQuery(id+"F0.wireOp",EDGE,"E0");var subQ2=makeQuery(id+"F0.imprint","INTERSECT",VERTEX,{"derivedFrom":[subQ1,subQ0]});Q118=makeQuery(id+"F0.imprint","IMPRINT",FACE,{"disambiguationData":[TD([[makeQuery(id+"F0.imprint","IMPRINT",EDGE,{"disambiguationData":[TD([[subQ2,-1.0]])],"derivedFrom":subQ1}),-1.0]])]});}
            var Q119;
            {var subQ0=sQuery(id+"F0.wireOp",EDGE,"E4.8.2");var subQ1=sQuery(id+"F0.wireOp",EDGE,"E0");var subQ2=makeQuery(id+"F0.imprint","INTERSECT",VERTEX,{"derivedFrom":[subQ1,subQ0]});Q119=makeQuery(id+"F0.imprint","IMPRINT",FACE,{"disambiguationData":[TD([[makeQuery(id+"F0.imprint","IMPRINT",EDGE,{"disambiguationData":[TD([[subQ2,-1.0]])],"derivedFrom":subQ1}),-1.0]])]});}
            var Q120;
            {var subQ0=sQuery(id+"F0.wireOp",EDGE,"E4.39.0");var subQ1=sQuery(id+"F0.wireOp",EDGE,"E0");var subQ2=makeQuery(id+"F0.imprint","INTERSECT",VERTEX,{"disambiguationData":[OD(0.0)],"derivedFrom":[subQ1,subQ0]});Q120=makeQuery(id+"F0.imprint","IMPRINT",FACE,{"disambiguationData":[TD([[makeQuery(id+"F0.imprint","IMPRINT",EDGE,{"disambiguationData":[TD([[subQ2,1.0]])],"derivedFrom":subQ1}),1.0]])]});}
            var Q121;
            {var subQ0=sQuery(id+"F0.wireOp",EDGE,"E4.14.2");var subQ1=sQuery(id+"F0.wireOp",EDGE,"E0");var subQ2=makeQuery(id+"F0.imprint","INTERSECT",VERTEX,{"derivedFrom":[subQ1,subQ0]});Q121=makeQuery(id+"F0.imprint","IMPRINT",FACE,{"disambiguationData":[TD([[makeQuery(id+"F0.imprint","IMPRINT",EDGE,{"disambiguationData":[TD([[subQ2,-1.0]])],"derivedFrom":subQ1}),-1.0]])]});}
            var Q122;
            {var subQ0=sQuery(id+"F0.wireOp",EDGE,"E4.22.0");var subQ1=sQuery(id+"F0.wireOp",EDGE,"E0");var subQ2=makeQuery(id+"F0.imprint","INTERSECT",VERTEX,{"disambiguationData":[OD(1.0)],"derivedFrom":[subQ1,subQ0]});Q122=makeQuery(id+"F0.imprint","IMPRINT",FACE,{"disambiguationData":[TD([[makeQuery(id+"F0.imprint","IMPRINT",EDGE,{"disambiguationData":[TD([[subQ2,1.0]])],"derivedFrom":subQ1}),-1.0]])]});}
            var Q123;
            {var subQ0=sQuery(id+"F0.wireOp",EDGE,"E4.33.0");var subQ1=sQuery(id+"F0.wireOp",EDGE,"E0");var subQ2=makeQuery(id+"F0.imprint","INTERSECT",VERTEX,{"disambiguationData":[OD(0.0)],"derivedFrom":[subQ1,subQ0]});Q123=makeQuery(id+"F0.imprint","IMPRINT",FACE,{"disambiguationData":[TD([[makeQuery(id+"F0.imprint","IMPRINT",EDGE,{"disambiguationData":[TD([[subQ2,1.0]])],"derivedFrom":subQ1}),1.0]])]});}
            var Q124;
            {var subQ0=sQuery(id+"F0.wireOp",EDGE,"E4.5.2");var subQ1=sQuery(id+"F0.wireOp",EDGE,"E0");var subQ2=makeQuery(id+"F0.imprint","INTERSECT",VERTEX,{"derivedFrom":[subQ1,subQ0]});Q124=makeQuery(id+"F0.imprint","IMPRINT",FACE,{"disambiguationData":[TD([[makeQuery(id+"F0.imprint","IMPRINT",EDGE,{"disambiguationData":[TD([[subQ2,-1.0]])],"derivedFrom":subQ1}),-1.0]])]});}
            var Q125;
            {var subQ0=sQuery(id+"F0.wireOp",EDGE,"E4.13.0");var subQ1=sQuery(id+"F0.wireOp",EDGE,"E0");var subQ2=makeQuery(id+"F0.imprint","INTERSECT",VERTEX,{"disambiguationData":[OD(1.0)],"derivedFrom":[subQ1,subQ0]});Q125=makeQuery(id+"F0.imprint","IMPRINT",FACE,{"disambiguationData":[TD([[makeQuery(id+"F0.imprint","IMPRINT",EDGE,{"disambiguationData":[TD([[subQ2,1.0]])],"derivedFrom":subQ1}),-1.0]])]});}
            var Q126;
            {var subQ0=sQuery(id+"F0.wireOp",EDGE,"E4.5.0");var subQ1=sQuery(id+"F0.wireOp",EDGE,"E0");var subQ2=makeQuery(id+"F0.imprint","INTERSECT",VERTEX,{"disambiguationData":[OD(0.0)],"derivedFrom":[subQ1,subQ0]});Q126=makeQuery(id+"F0.imprint","IMPRINT",FACE,{"disambiguationData":[TD([[makeQuery(id+"F0.imprint","IMPRINT",EDGE,{"disambiguationData":[TD([[subQ2,1.0]])],"derivedFrom":subQ1}),1.0]])]});}
            var Q127;
            {var subQ0=sQuery(id+"F0.wireOp",EDGE,"E4.14.0");var subQ1=sQuery(id+"F0.wireOp",EDGE,"E0");var subQ2=makeQuery(id+"F0.imprint","INTERSECT",VERTEX,{"disambiguationData":[OD(1.0)],"derivedFrom":[subQ1,subQ0]});Q127=makeQuery(id+"F0.imprint","IMPRINT",FACE,{"disambiguationData":[TD([[makeQuery(id+"F0.imprint","IMPRINT",EDGE,{"disambiguationData":[TD([[subQ2,1.0]])],"derivedFrom":subQ1}),-1.0]])]});}
            var Q128;
            {var subQ0=sQuery(id+"F0.wireOp",EDGE,"E4.35.0");var subQ1=sQuery(id+"F0.wireOp",EDGE,"E0");var subQ2=makeQuery(id+"F0.imprint","INTERSECT",VERTEX,{"disambiguationData":[OD(0.0)],"derivedFrom":[subQ1,subQ0]});Q128=makeQuery(id+"F0.imprint","IMPRINT",FACE,{"disambiguationData":[TD([[makeQuery(id+"F0.imprint","IMPRINT",EDGE,{"disambiguationData":[TD([[subQ2,1.0]])],"derivedFrom":subQ1}),1.0]])]});}
            var Q129;
            {var subQ0=sQuery(id+"F0.wireOp",EDGE,"E4.4.2");var subQ1=sQuery(id+"F0.wireOp",EDGE,"E0");var subQ2=makeQuery(id+"F0.imprint","INTERSECT",VERTEX,{"derivedFrom":[subQ1,subQ0]});Q129=makeQuery(id+"F0.imprint","IMPRINT",FACE,{"disambiguationData":[TD([[makeQuery(id+"F0.imprint","IMPRINT",EDGE,{"disambiguationData":[TD([[subQ2,-1.0]])],"derivedFrom":subQ1}),-1.0]])]});}
            var Q130;
            {var subQ0=sQuery(id+"F0.wireOp",EDGE,"E4.18.2");var subQ1=sQuery(id+"F0.wireOp",EDGE,"E0");var subQ2=makeQuery(id+"F0.imprint","INTERSECT",VERTEX,{"derivedFrom":[subQ1,subQ0]});Q130=makeQuery(id+"F0.imprint","IMPRINT",FACE,{"disambiguationData":[TD([[makeQuery(id+"F0.imprint","IMPRINT",EDGE,{"disambiguationData":[TD([[subQ2,-1.0]])],"derivedFrom":subQ1}),-1.0]])]});}
            var Q131;
            {var subQ0=sQuery(id+"F0.wireOp",EDGE,"E4.10.0");var subQ1=sQuery(id+"F0.wireOp",EDGE,"E0");var subQ2=makeQuery(id+"F0.imprint","INTERSECT",VERTEX,{"disambiguationData":[OD(0.0)],"derivedFrom":[subQ1,subQ0]});Q131=makeQuery(id+"F0.imprint","IMPRINT",FACE,{"disambiguationData":[TD([[makeQuery(id+"F0.imprint","IMPRINT",EDGE,{"disambiguationData":[TD([[subQ2,1.0]])],"derivedFrom":subQ1}),1.0]])]});}
            var Q132;
            {var subQ0=sQuery(id+"F0.wireOp",EDGE,"E4.37.0");var subQ1=sQuery(id+"F0.wireOp",EDGE,"E0");var subQ2=makeQuery(id+"F0.imprint","INTERSECT",VERTEX,{"disambiguationData":[OD(1.0)],"derivedFrom":[subQ1,subQ0]});Q132=makeQuery(id+"F0.imprint","IMPRINT",FACE,{"disambiguationData":[TD([[makeQuery(id+"F0.imprint","IMPRINT",EDGE,{"disambiguationData":[TD([[subQ2,1.0]])],"derivedFrom":subQ1}),-1.0]])]});}
            var Q133;
            {var subQ0=sQuery(id+"F0.wireOp",EDGE,"E4.3.0");var subQ1=sQuery(id+"F0.wireOp",EDGE,"E0");var subQ2=makeQuery(id+"F0.imprint","INTERSECT",VERTEX,{"disambiguationData":[OD(1.0)],"derivedFrom":[subQ1,subQ0]});Q133=makeQuery(id+"F0.imprint","IMPRINT",FACE,{"disambiguationData":[TD([[makeQuery(id+"F0.imprint","IMPRINT",EDGE,{"disambiguationData":[TD([[subQ2,1.0]])],"derivedFrom":subQ1}),-1.0]])]});}
            var Q134;
            {var subQ0=sQuery(id+"F0.wireOp",EDGE,"E4.10.2");var subQ1=sQuery(id+"F0.wireOp",EDGE,"E0");var subQ2=makeQuery(id+"F0.imprint","INTERSECT",VERTEX,{"derivedFrom":[subQ1,subQ0]});Q134=makeQuery(id+"F0.imprint","IMPRINT",FACE,{"disambiguationData":[TD([[makeQuery(id+"F0.imprint","IMPRINT",EDGE,{"disambiguationData":[TD([[subQ2,-1.0]])],"derivedFrom":subQ1}),-1.0]])]});}
            var Q135;
            {var subQ0=sQuery(id+"F0.wireOp",EDGE,"E4.7.0");var subQ1=sQuery(id+"F0.wireOp",EDGE,"E0");var subQ2=makeQuery(id+"F0.imprint","INTERSECT",VERTEX,{"disambiguationData":[OD(1.0)],"derivedFrom":[subQ1,subQ0]});Q135=makeQuery(id+"F0.imprint","IMPRINT",FACE,{"disambiguationData":[TD([[makeQuery(id+"F0.imprint","IMPRINT",EDGE,{"disambiguationData":[TD([[subQ2,1.0]])],"derivedFrom":subQ1}),-1.0]])]});}
            var Q136;
            {var subQ0=sQuery(id+"F0.wireOp",EDGE,"E4.6.0");var subQ1=sQuery(id+"F0.wireOp",EDGE,"E0");var subQ2=makeQuery(id+"F0.imprint","INTERSECT",VERTEX,{"disambiguationData":[OD(1.0)],"derivedFrom":[subQ1,subQ0]});Q136=makeQuery(id+"F0.imprint","IMPRINT",FACE,{"disambiguationData":[TD([[makeQuery(id+"F0.imprint","IMPRINT",EDGE,{"disambiguationData":[TD([[subQ2,1.0]])],"derivedFrom":subQ1}),-1.0]])]});}
            var Q137;
            {var subQ0=sQuery(id+"F0.wireOp",EDGE,"E4.2.0");var subQ1=sQuery(id+"F0.wireOp",EDGE,"E0");var subQ2=makeQuery(id+"F0.imprint","INTERSECT",VERTEX,{"disambiguationData":[OD(1.0)],"derivedFrom":[subQ1,subQ0]});Q137=makeQuery(id+"F0.imprint","IMPRINT",FACE,{"disambiguationData":[TD([[makeQuery(id+"F0.imprint","IMPRINT",EDGE,{"disambiguationData":[TD([[subQ2,1.0]])],"derivedFrom":subQ1}),-1.0]])]});}
            var Q138;
            {var subQ0=sQuery(id+"F0.wireOp",EDGE,"E4.33.0");var subQ1=sQuery(id+"F0.wireOp",EDGE,"E0");var subQ2=makeQuery(id+"F0.imprint","INTERSECT",VERTEX,{"disambiguationData":[OD(1.0)],"derivedFrom":[subQ1,subQ0]});Q138=makeQuery(id+"F0.imprint","IMPRINT",FACE,{"disambiguationData":[TD([[makeQuery(id+"F0.imprint","IMPRINT",EDGE,{"disambiguationData":[TD([[subQ2,1.0]])],"derivedFrom":subQ1}),-1.0]])]});}
            var Q139;
            {var subQ0=sQuery(id+"F0.wireOp",EDGE,"E4.10.0");var subQ1=sQuery(id+"F0.wireOp",EDGE,"E0");var subQ2=makeQuery(id+"F0.imprint","INTERSECT",VERTEX,{"disambiguationData":[OD(1.0)],"derivedFrom":[subQ1,subQ0]});Q139=makeQuery(id+"F0.imprint","IMPRINT",FACE,{"disambiguationData":[TD([[makeQuery(id+"F0.imprint","IMPRINT",EDGE,{"disambiguationData":[TD([[subQ2,1.0]])],"derivedFrom":subQ1}),-1.0]])]});}
            var Q140;
            {var subQ0=sQuery(id+"F0.wireOp",EDGE,"E4.16.0");var subQ1=sQuery(id+"F0.wireOp",EDGE,"E0");var subQ2=makeQuery(id+"F0.imprint","INTERSECT",VERTEX,{"disambiguationData":[OD(0.0)],"derivedFrom":[subQ1,subQ0]});Q140=makeQuery(id+"F0.imprint","IMPRINT",FACE,{"disambiguationData":[TD([[makeQuery(id+"F0.imprint","IMPRINT",EDGE,{"disambiguationData":[TD([[subQ2,1.0]])],"derivedFrom":subQ1}),1.0]])]});}
            var Q141;
            {var subQ0=sQuery(id+"F0.wireOp",EDGE,"E4.19.0");var subQ1=sQuery(id+"F0.wireOp",EDGE,"E0");var subQ2=makeQuery(id+"F0.imprint","INTERSECT",VERTEX,{"disambiguationData":[OD(1.0)],"derivedFrom":[subQ1,subQ0]});Q141=makeQuery(id+"F0.imprint","IMPRINT",FACE,{"disambiguationData":[TD([[makeQuery(id+"F0.imprint","IMPRINT",EDGE,{"disambiguationData":[TD([[subQ2,1.0]])],"derivedFrom":subQ1}),-1.0]])]});}
            var Q142;
            {var subQ0=sQuery(id+"F0.wireOp",EDGE,"E4.29.0");var subQ1=sQuery(id+"F0.wireOp",EDGE,"E0");var subQ2=makeQuery(id+"F0.imprint","INTERSECT",VERTEX,{"disambiguationData":[OD(1.0)],"derivedFrom":[subQ1,subQ0]});Q142=makeQuery(id+"F0.imprint","IMPRINT",FACE,{"disambiguationData":[TD([[makeQuery(id+"F0.imprint","IMPRINT",EDGE,{"disambiguationData":[TD([[subQ2,1.0]])],"derivedFrom":subQ1}),-1.0]])]});}
            var Q143;
            {var subQ0=sQuery(id+"F0.wireOp",EDGE,"E4.31.0");var subQ1=sQuery(id+"F0.wireOp",EDGE,"E0");var subQ2=makeQuery(id+"F0.imprint","INTERSECT",VERTEX,{"disambiguationData":[OD(0.0)],"derivedFrom":[subQ1,subQ0]});Q143=makeQuery(id+"F0.imprint","IMPRINT",FACE,{"disambiguationData":[TD([[makeQuery(id+"F0.imprint","IMPRINT",EDGE,{"disambiguationData":[TD([[subQ2,1.0]])],"derivedFrom":subQ1}),1.0]])]});}
            var Q144;
            {var subQ0=sQuery(id+"F0.wireOp",EDGE,"E4.30.0");var subQ1=sQuery(id+"F0.wireOp",EDGE,"E0");var subQ2=makeQuery(id+"F0.imprint","INTERSECT",VERTEX,{"disambiguationData":[OD(0.0)],"derivedFrom":[subQ1,subQ0]});Q144=makeQuery(id+"F0.imprint","IMPRINT",FACE,{"disambiguationData":[TD([[makeQuery(id+"F0.imprint","IMPRINT",EDGE,{"disambiguationData":[TD([[subQ2,1.0]])],"derivedFrom":subQ1}),1.0]])]});}
            var Q145;
            {var subQ0=sQuery(id+"F0.wireOp",EDGE,"E4.3.0");var subQ1=sQuery(id+"F0.wireOp",EDGE,"E0");var subQ2=makeQuery(id+"F0.imprint","INTERSECT",VERTEX,{"disambiguationData":[OD(0.0)],"derivedFrom":[subQ1,subQ0]});Q145=makeQuery(id+"F0.imprint","IMPRINT",FACE,{"disambiguationData":[TD([[makeQuery(id+"F0.imprint","IMPRINT",EDGE,{"disambiguationData":[TD([[subQ2,1.0]])],"derivedFrom":subQ1}),1.0]])]});}
            var Q146;
            {var subQ0=sQuery(id+"F0.wireOp",EDGE,"E4.9.2");var subQ1=sQuery(id+"F0.wireOp",EDGE,"E0");var subQ2=makeQuery(id+"F0.imprint","INTERSECT",VERTEX,{"derivedFrom":[subQ1,subQ0]});Q146=makeQuery(id+"F0.imprint","IMPRINT",FACE,{"disambiguationData":[TD([[makeQuery(id+"F0.imprint","IMPRINT",EDGE,{"disambiguationData":[TD([[subQ2,-1.0]])],"derivedFrom":subQ1}),-1.0]])]});}
            var Q147;
            {var subQ0=sQuery(id+"F0.wireOp",EDGE,"E2");var subQ1=sQuery(id+"F0.wireOp",EDGE,"E0");var subQ2=makeQuery(id+"F0.imprint","INTERSECT",VERTEX,{"disambiguationData":[OD(1.0)],"derivedFrom":[subQ1,subQ0]});Q147=makeQuery(id+"F0.imprint","IMPRINT",FACE,{"disambiguationData":[TD([[makeQuery(id+"F0.imprint","IMPRINT",EDGE,{"disambiguationData":[TD([[subQ2,1.0]])],"derivedFrom":subQ1}),-1.0]])]});}
            var Q148;
            {var subQ0=sQuery(id+"F0.wireOp",EDGE,"E4.4.0");var subQ1=sQuery(id+"F0.wireOp",EDGE,"E0");var subQ2=makeQuery(id+"F0.imprint","INTERSECT",VERTEX,{"disambiguationData":[OD(1.0)],"derivedFrom":[subQ1,subQ0]});Q148=makeQuery(id+"F0.imprint","IMPRINT",FACE,{"disambiguationData":[TD([[makeQuery(id+"F0.imprint","IMPRINT",EDGE,{"disambiguationData":[TD([[subQ2,1.0]])],"derivedFrom":subQ1}),-1.0]])]});}
            var Q149;
            {var subQ0=sQuery(id+"F0.wireOp",EDGE,"E4.24.2");var subQ1=sQuery(id+"F0.wireOp",EDGE,"E0");var subQ2=makeQuery(id+"F0.imprint","INTERSECT",VERTEX,{"derivedFrom":[subQ1,subQ0]});Q149=makeQuery(id+"F0.imprint","IMPRINT",FACE,{"disambiguationData":[TD([[makeQuery(id+"F0.imprint","IMPRINT",EDGE,{"disambiguationData":[TD([[subQ2,-1.0]])],"derivedFrom":subQ1}),-1.0]])]});}
            var Q150;
            {var subQ0=sQuery(id+"F0.wireOp",EDGE,"E4.26.2");var subQ1=sQuery(id+"F0.wireOp",EDGE,"E0");var subQ2=makeQuery(id+"F0.imprint","INTERSECT",VERTEX,{"derivedFrom":[subQ1,subQ0]});Q150=makeQuery(id+"F0.imprint","IMPRINT",FACE,{"disambiguationData":[TD([[makeQuery(id+"F0.imprint","IMPRINT",EDGE,{"disambiguationData":[TD([[subQ2,-1.0]])],"derivedFrom":subQ1}),-1.0]])]});}
            var Q151;
            {var subQ0=sQuery(id+"F0.wireOp",EDGE,"E4.27.2");var subQ1=sQuery(id+"F0.wireOp",EDGE,"E0");var subQ2=makeQuery(id+"F0.imprint","INTERSECT",VERTEX,{"derivedFrom":[subQ1,subQ0]});Q151=makeQuery(id+"F0.imprint","IMPRINT",FACE,{"disambiguationData":[TD([[makeQuery(id+"F0.imprint","IMPRINT",EDGE,{"disambiguationData":[TD([[subQ2,-1.0]])],"derivedFrom":subQ1}),-1.0]])]});}
            var Q152;
            {var subQ0=sQuery(id+"F0.wireOp",EDGE,"E4.9.0");var subQ1=sQuery(id+"F0.wireOp",EDGE,"E0");var subQ2=makeQuery(id+"F0.imprint","INTERSECT",VERTEX,{"disambiguationData":[OD(1.0)],"derivedFrom":[subQ1,subQ0]});Q152=makeQuery(id+"F0.imprint","IMPRINT",FACE,{"disambiguationData":[TD([[makeQuery(id+"F0.imprint","IMPRINT",EDGE,{"disambiguationData":[TD([[subQ2,1.0]])],"derivedFrom":subQ1}),-1.0]])]});}
            var Q153;
            {var subQ0=sQuery(id+"F0.wireOp",EDGE,"E4.13.2");var subQ1=sQuery(id+"F0.wireOp",EDGE,"E0");var subQ2=makeQuery(id+"F0.imprint","INTERSECT",VERTEX,{"derivedFrom":[subQ1,subQ0]});Q153=makeQuery(id+"F0.imprint","IMPRINT",FACE,{"disambiguationData":[TD([[makeQuery(id+"F0.imprint","IMPRINT",EDGE,{"disambiguationData":[TD([[subQ2,-1.0]])],"derivedFrom":subQ1}),-1.0]])]});}
            var Q154;
            {var subQ0=sQuery(id+"F0.wireOp",EDGE,"E4.15.2");var subQ1=sQuery(id+"F0.wireOp",EDGE,"E0");var subQ2=makeQuery(id+"F0.imprint","INTERSECT",VERTEX,{"derivedFrom":[subQ1,subQ0]});Q154=makeQuery(id+"F0.imprint","IMPRINT",FACE,{"disambiguationData":[TD([[makeQuery(id+"F0.imprint","IMPRINT",EDGE,{"disambiguationData":[TD([[subQ2,-1.0]])],"derivedFrom":subQ1}),-1.0]])]});}
            var Q155;
            {var subQ0=sQuery(id+"F0.wireOp",EDGE,"E4.23.0");var subQ1=sQuery(id+"F0.wireOp",EDGE,"E0");var subQ2=makeQuery(id+"F0.imprint","INTERSECT",VERTEX,{"disambiguationData":[OD(1.0)],"derivedFrom":[subQ1,subQ0]});Q155=makeQuery(id+"F0.imprint","IMPRINT",FACE,{"disambiguationData":[TD([[makeQuery(id+"F0.imprint","IMPRINT",EDGE,{"disambiguationData":[TD([[subQ2,1.0]])],"derivedFrom":subQ1}),-1.0]])]});}
            var Q156;
            {var subQ0=sQuery(id+"F0.wireOp",EDGE,"E4.31.0");var subQ1=sQuery(id+"F0.wireOp",EDGE,"E0");var subQ2=makeQuery(id+"F0.imprint","INTERSECT",VERTEX,{"disambiguationData":[OD(1.0)],"derivedFrom":[subQ1,subQ0]});Q156=makeQuery(id+"F0.imprint","IMPRINT",FACE,{"disambiguationData":[TD([[makeQuery(id+"F0.imprint","IMPRINT",EDGE,{"disambiguationData":[TD([[subQ2,1.0]])],"derivedFrom":subQ1}),-1.0]])]});}
            var Q157;
            {var subQ0=sQuery(id+"F0.wireOp",EDGE,"E4.1.0");var subQ1=sQuery(id+"F0.wireOp",EDGE,"E0");var subQ2=makeQuery(id+"F0.imprint","INTERSECT",VERTEX,{"disambiguationData":[OD(1.0)],"derivedFrom":[subQ1,subQ0]});Q157=makeQuery(id+"F0.imprint","IMPRINT",FACE,{"disambiguationData":[TD([[makeQuery(id+"F0.imprint","IMPRINT",EDGE,{"disambiguationData":[TD([[subQ2,1.0]])],"derivedFrom":subQ1}),-1.0]])]});}
            var Q158;
            {var subQ0=sQuery(id+"F0.wireOp",EDGE,"E4.33.2");var subQ1=sQuery(id+"F0.wireOp",EDGE,"E0");var subQ2=makeQuery(id+"F0.imprint","INTERSECT",VERTEX,{"derivedFrom":[subQ1,subQ0]});Q158=makeQuery(id+"F0.imprint","IMPRINT",FACE,{"disambiguationData":[TD([[makeQuery(id+"F0.imprint","IMPRINT",EDGE,{"disambiguationData":[TD([[subQ2,-1.0]])],"derivedFrom":subQ1}),-1.0]])]});}
            var Q159;
            {var subQ0=sQuery(id+"F0.wireOp",EDGE,"E4.20.2");var subQ1=sQuery(id+"F0.wireOp",EDGE,"E0");var subQ2=makeQuery(id+"F0.imprint","INTERSECT",VERTEX,{"derivedFrom":[subQ1,subQ0]});Q159=makeQuery(id+"F0.imprint","IMPRINT",FACE,{"disambiguationData":[TD([[makeQuery(id+"F0.imprint","IMPRINT",EDGE,{"disambiguationData":[TD([[subQ2,-1.0]])],"derivedFrom":subQ1}),-1.0]])]});}
            var Q160;
            {var subQ0=sQuery(id+"F0.wireOp",EDGE,"E4.5.0");var subQ1=sQuery(id+"F0.wireOp",EDGE,"E0");var subQ2=makeQuery(id+"F0.imprint","INTERSECT",VERTEX,{"disambiguationData":[OD(1.0)],"derivedFrom":[subQ1,subQ0]});Q160=makeQuery(id+"F0.imprint","IMPRINT",FACE,{"disambiguationData":[TD([[makeQuery(id+"F0.imprint","IMPRINT",EDGE,{"disambiguationData":[TD([[subQ2,1.0]])],"derivedFrom":subQ1}),-1.0]])]});}
            var Q161;
            {var subQ0=sQuery(id+"F0.wireOp",EDGE,"E4.37.2");var subQ1=sQuery(id+"F0.wireOp",EDGE,"E0");var subQ2=makeQuery(id+"F0.imprint","INTERSECT",VERTEX,{"derivedFrom":[subQ1,subQ0]});Q161=makeQuery(id+"F0.imprint","IMPRINT",FACE,{"disambiguationData":[TD([[makeQuery(id+"F0.imprint","IMPRINT",EDGE,{"disambiguationData":[TD([[subQ2,-1.0]])],"derivedFrom":subQ1}),-1.0]])]});}
            var Q162;
            {var subQ0=sQuery(id+"F0.wireOp",EDGE,"E4.30.2");var subQ1=sQuery(id+"F0.wireOp",EDGE,"E0");var subQ2=makeQuery(id+"F0.imprint","INTERSECT",VERTEX,{"derivedFrom":[subQ1,subQ0]});Q162=makeQuery(id+"F0.imprint","IMPRINT",FACE,{"disambiguationData":[TD([[makeQuery(id+"F0.imprint","IMPRINT",EDGE,{"disambiguationData":[TD([[subQ2,-1.0]])],"derivedFrom":subQ1}),-1.0]])]});}
            var Q163;
            {var subQ0=sQuery(id+"F0.wireOp",EDGE,"E4.31.2");var subQ1=sQuery(id+"F0.wireOp",EDGE,"E0");var subQ2=makeQuery(id+"F0.imprint","INTERSECT",VERTEX,{"derivedFrom":[subQ1,subQ0]});Q163=makeQuery(id+"F0.imprint","IMPRINT",FACE,{"disambiguationData":[TD([[makeQuery(id+"F0.imprint","IMPRINT",EDGE,{"disambiguationData":[TD([[subQ2,-1.0]])],"derivedFrom":subQ1}),-1.0]])]});}
            var Q164;
            {var subQ0=sQuery(id+"F0.wireOp",EDGE,"E4.7.0");var subQ1=sQuery(id+"F0.wireOp",EDGE,"E0");var subQ2=makeQuery(id+"F0.imprint","INTERSECT",VERTEX,{"disambiguationData":[OD(0.0)],"derivedFrom":[subQ1,subQ0]});Q164=makeQuery(id+"F0.imprint","IMPRINT",FACE,{"disambiguationData":[TD([[makeQuery(id+"F0.imprint","IMPRINT",EDGE,{"disambiguationData":[TD([[subQ2,1.0]])],"derivedFrom":subQ1}),1.0]])]});}
            var Q165;
            {var subQ0=sQuery(id+"F0.wireOp",EDGE,"E4.8.0");var subQ1=sQuery(id+"F0.wireOp",EDGE,"E0");var subQ2=makeQuery(id+"F0.imprint","INTERSECT",VERTEX,{"disambiguationData":[OD(0.0)],"derivedFrom":[subQ1,subQ0]});Q165=makeQuery(id+"F0.imprint","IMPRINT",FACE,{"disambiguationData":[TD([[makeQuery(id+"F0.imprint","IMPRINT",EDGE,{"disambiguationData":[TD([[subQ2,1.0]])],"derivedFrom":subQ1}),1.0]])]});}
            var Q166;
            {var subQ0=sQuery(id+"F0.wireOp",EDGE,"E4.34.2");var subQ1=sQuery(id+"F0.wireOp",EDGE,"E0");var subQ2=makeQuery(id+"F0.imprint","INTERSECT",VERTEX,{"derivedFrom":[subQ1,subQ0]});Q166=makeQuery(id+"F0.imprint","IMPRINT",FACE,{"disambiguationData":[TD([[makeQuery(id+"F0.imprint","IMPRINT",EDGE,{"disambiguationData":[TD([[subQ2,-1.0]])],"derivedFrom":subQ1}),-1.0]])]});}
            var Q167;
            {var subQ0=sQuery(id+"F0.wireOp",EDGE,"E4.38.0");var subQ1=sQuery(id+"F0.wireOp",EDGE,"E0");var subQ2=makeQuery(id+"F0.imprint","INTERSECT",VERTEX,{"disambiguationData":[OD(0.0)],"derivedFrom":[subQ1,subQ0]});Q167=makeQuery(id+"F0.imprint","IMPRINT",FACE,{"disambiguationData":[TD([[makeQuery(id+"F0.imprint","IMPRINT",EDGE,{"disambiguationData":[TD([[subQ2,1.0]])],"derivedFrom":subQ1}),1.0]])]});}
            var Q168;
            {var subQ0=sQuery(id+"F0.wireOp",EDGE,"E4.25.0");var subQ1=sQuery(id+"F0.wireOp",EDGE,"E0");var subQ2=makeQuery(id+"F0.imprint","INTERSECT",VERTEX,{"disambiguationData":[OD(1.0)],"derivedFrom":[subQ1,subQ0]});Q168=makeQuery(id+"F0.imprint","IMPRINT",FACE,{"disambiguationData":[TD([[makeQuery(id+"F0.imprint","IMPRINT",EDGE,{"disambiguationData":[TD([[subQ2,1.0]])],"derivedFrom":subQ1}),-1.0]])]});}
            var Q169;
            {var subQ0=sQuery(id+"F0.wireOp",EDGE,"E4.18.0");var subQ1=sQuery(id+"F0.wireOp",EDGE,"E0");var subQ2=makeQuery(id+"F0.imprint","INTERSECT",VERTEX,{"disambiguationData":[OD(0.0)],"derivedFrom":[subQ1,subQ0]});Q169=makeQuery(id+"F0.imprint","IMPRINT",FACE,{"disambiguationData":[TD([[makeQuery(id+"F0.imprint","IMPRINT",EDGE,{"disambiguationData":[TD([[subQ2,1.0]])],"derivedFrom":subQ1}),1.0]])]});}
            var Q170;
            {var subQ0=sQuery(id+"F0.wireOp",EDGE,"E4.28.0");var subQ1=sQuery(id+"F0.wireOp",EDGE,"E0");var subQ2=makeQuery(id+"F0.imprint","INTERSECT",VERTEX,{"disambiguationData":[OD(0.0)],"derivedFrom":[subQ1,subQ0]});Q170=makeQuery(id+"F0.imprint","IMPRINT",FACE,{"disambiguationData":[TD([[makeQuery(id+"F0.imprint","IMPRINT",EDGE,{"disambiguationData":[TD([[subQ2,1.0]])],"derivedFrom":subQ1}),1.0]])]});}
            var Q171;
            {var subQ0=sQuery(id+"F0.wireOp",EDGE,"E4.36.2");var subQ1=sQuery(id+"F0.wireOp",EDGE,"E0");var subQ2=makeQuery(id+"F0.imprint","INTERSECT",VERTEX,{"derivedFrom":[subQ1,subQ0]});Q171=makeQuery(id+"F0.imprint","IMPRINT",FACE,{"disambiguationData":[TD([[makeQuery(id+"F0.imprint","IMPRINT",EDGE,{"disambiguationData":[TD([[subQ2,-1.0]])],"derivedFrom":subQ1}),-1.0]])]});}
            var Q172;
            {var subQ0=sQuery(id+"F0.wireOp",EDGE,"E4.35.0");var subQ1=sQuery(id+"F0.wireOp",EDGE,"E0");var subQ2=makeQuery(id+"F0.imprint","INTERSECT",VERTEX,{"disambiguationData":[OD(1.0)],"derivedFrom":[subQ1,subQ0]});Q172=makeQuery(id+"F0.imprint","IMPRINT",FACE,{"disambiguationData":[TD([[makeQuery(id+"F0.imprint","IMPRINT",EDGE,{"disambiguationData":[TD([[subQ2,1.0]])],"derivedFrom":subQ1}),-1.0]])]});}
            var Q173;
            {var subQ0=sQuery(id+"F0.wireOp",EDGE,"E4.13.0");var subQ1=sQuery(id+"F0.wireOp",EDGE,"E0");var subQ2=makeQuery(id+"F0.imprint","INTERSECT",VERTEX,{"disambiguationData":[OD(0.0)],"derivedFrom":[subQ1,subQ0]});Q173=makeQuery(id+"F0.imprint","IMPRINT",FACE,{"disambiguationData":[TD([[makeQuery(id+"F0.imprint","IMPRINT",EDGE,{"disambiguationData":[TD([[subQ2,1.0]])],"derivedFrom":subQ1}),1.0]])]});}
            var Q174;
            {var subQ0=sQuery(id+"F0.wireOp",EDGE,"E4.20.0");var subQ1=sQuery(id+"F0.wireOp",EDGE,"E0");var subQ2=makeQuery(id+"F0.imprint","INTERSECT",VERTEX,{"disambiguationData":[OD(1.0)],"derivedFrom":[subQ1,subQ0]});Q174=makeQuery(id+"F0.imprint","IMPRINT",FACE,{"disambiguationData":[TD([[makeQuery(id+"F0.imprint","IMPRINT",EDGE,{"disambiguationData":[TD([[subQ2,1.0]])],"derivedFrom":subQ1}),-1.0]])]});}
            var Q175;
            {var subQ0=sQuery(id+"F0.wireOp",EDGE,"E4.29.0");var subQ1=sQuery(id+"F0.wireOp",EDGE,"E0");var subQ2=makeQuery(id+"F0.imprint","INTERSECT",VERTEX,{"disambiguationData":[OD(0.0)],"derivedFrom":[subQ1,subQ0]});Q175=makeQuery(id+"F0.imprint","IMPRINT",FACE,{"disambiguationData":[TD([[makeQuery(id+"F0.imprint","IMPRINT",EDGE,{"disambiguationData":[TD([[subQ2,1.0]])],"derivedFrom":subQ1}),1.0]])]});}
            var Q176;
            {var subQ0=sQuery(id+"F0.wireOp",EDGE,"E4.1.0");var subQ1=sQuery(id+"F0.wireOp",EDGE,"E0");var subQ2=makeQuery(id+"F0.imprint","INTERSECT",VERTEX,{"disambiguationData":[OD(0.0)],"derivedFrom":[subQ1,subQ0]});Q176=makeQuery(id+"F0.imprint","IMPRINT",FACE,{"disambiguationData":[TD([[makeQuery(id+"F0.imprint","IMPRINT",EDGE,{"disambiguationData":[TD([[subQ2,1.0]])],"derivedFrom":subQ1}),1.0]])]});}
            var Q177;
            {var subQ0=sQuery(id+"F0.wireOp",EDGE,"E4.17.0");var subQ1=sQuery(id+"F0.wireOp",EDGE,"E0");var subQ2=makeQuery(id+"F0.imprint","INTERSECT",VERTEX,{"disambiguationData":[OD(0.0)],"derivedFrom":[subQ1,subQ0]});Q177=makeQuery(id+"F0.imprint","IMPRINT",FACE,{"disambiguationData":[TD([[makeQuery(id+"F0.imprint","IMPRINT",EDGE,{"disambiguationData":[TD([[subQ2,1.0]])],"derivedFrom":subQ1}),1.0]])]});}
            var Q178;
            {var subQ0=sQuery(id+"F0.wireOp",EDGE,"E4.11.2");var subQ1=sQuery(id+"F0.wireOp",EDGE,"E0");var subQ2=makeQuery(id+"F0.imprint","INTERSECT",VERTEX,{"derivedFrom":[subQ1,subQ0]});Q178=makeQuery(id+"F0.imprint","IMPRINT",FACE,{"disambiguationData":[TD([[makeQuery(id+"F0.imprint","IMPRINT",EDGE,{"disambiguationData":[TD([[subQ2,-1.0]])],"derivedFrom":subQ1}),-1.0]])]});}
            var Q179;
            {var subQ0=sQuery(id+"F0.wireOp",EDGE,"E4.14.0");var subQ1=sQuery(id+"F0.wireOp",EDGE,"E0");var subQ2=makeQuery(id+"F0.imprint","INTERSECT",VERTEX,{"disambiguationData":[OD(0.0)],"derivedFrom":[subQ1,subQ0]});Q179=makeQuery(id+"F0.imprint","IMPRINT",FACE,{"disambiguationData":[TD([[makeQuery(id+"F0.imprint","IMPRINT",EDGE,{"disambiguationData":[TD([[subQ2,1.0]])],"derivedFrom":subQ1}),1.0]])]});}
            var Q180;
            {var subQ0=sQuery(id+"F0.wireOp",EDGE,"E4.12.0");var subQ1=sQuery(id+"F0.wireOp",EDGE,"E0");var subQ2=makeQuery(id+"F0.imprint","INTERSECT",VERTEX,{"disambiguationData":[OD(0.0)],"derivedFrom":[subQ1,subQ0]});Q180=makeQuery(id+"F0.imprint","IMPRINT",FACE,{"disambiguationData":[TD([[makeQuery(id+"F0.imprint","IMPRINT",EDGE,{"disambiguationData":[TD([[subQ2,1.0]])],"derivedFrom":subQ1}),1.0]])]});}
            var Q181;
            {var subQ0=sQuery(id+"F0.wireOp",EDGE,"E4.7.2");var subQ1=sQuery(id+"F0.wireOp",EDGE,"E0");var subQ2=makeQuery(id+"F0.imprint","INTERSECT",VERTEX,{"derivedFrom":[subQ1,subQ0]});Q181=makeQuery(id+"F0.imprint","IMPRINT",FACE,{"disambiguationData":[TD([[makeQuery(id+"F0.imprint","IMPRINT",EDGE,{"disambiguationData":[TD([[subQ2,-1.0]])],"derivedFrom":subQ1}),-1.0]])]});}
            var Q182;
            {var subQ0=sQuery(id+"F0.wireOp",EDGE,"E4.16.2");var subQ1=sQuery(id+"F0.wireOp",EDGE,"E0");var subQ2=makeQuery(id+"F0.imprint","INTERSECT",VERTEX,{"derivedFrom":[subQ1,subQ0]});Q182=makeQuery(id+"F0.imprint","IMPRINT",FACE,{"disambiguationData":[TD([[makeQuery(id+"F0.imprint","IMPRINT",EDGE,{"disambiguationData":[TD([[subQ2,-1.0]])],"derivedFrom":subQ1}),-1.0]])]});}
            var Q183;
            {var subQ0=sQuery(id+"F0.wireOp",EDGE,"E4.26.0");var subQ1=sQuery(id+"F0.wireOp",EDGE,"E0");var subQ2=makeQuery(id+"F0.imprint","INTERSECT",VERTEX,{"disambiguationData":[OD(1.0)],"derivedFrom":[subQ1,subQ0]});Q183=makeQuery(id+"F0.imprint","IMPRINT",FACE,{"disambiguationData":[TD([[makeQuery(id+"F0.imprint","IMPRINT",EDGE,{"disambiguationData":[TD([[subQ2,1.0]])],"derivedFrom":subQ1}),-1.0]])]});}
            var Q184;
            {var subQ0=sQuery(id+"F0.wireOp",EDGE,"E4.34.0");var subQ1=sQuery(id+"F0.wireOp",EDGE,"E0");var subQ2=makeQuery(id+"F0.imprint","INTERSECT",VERTEX,{"disambiguationData":[OD(1.0)],"derivedFrom":[subQ1,subQ0]});Q184=makeQuery(id+"F0.imprint","IMPRINT",FACE,{"disambiguationData":[TD([[makeQuery(id+"F0.imprint","IMPRINT",EDGE,{"disambiguationData":[TD([[subQ2,1.0]])],"derivedFrom":subQ1}),-1.0]])]});}
            var Q185;
            {var subQ0=sQuery(id+"F0.wireOp",EDGE,"E4.30.0");var subQ1=sQuery(id+"F0.wireOp",EDGE,"E0");var subQ2=makeQuery(id+"F0.imprint","INTERSECT",VERTEX,{"disambiguationData":[OD(1.0)],"derivedFrom":[subQ1,subQ0]});Q185=makeQuery(id+"F0.imprint","IMPRINT",FACE,{"disambiguationData":[TD([[makeQuery(id+"F0.imprint","IMPRINT",EDGE,{"disambiguationData":[TD([[subQ2,1.0]])],"derivedFrom":subQ1}),-1.0]])]});}
            var Q186;
            {var subQ0=sQuery(id+"F0.wireOp",EDGE,"E4.22.0");var subQ1=sQuery(id+"F0.wireOp",EDGE,"E0");var subQ2=makeQuery(id+"F0.imprint","INTERSECT",VERTEX,{"disambiguationData":[OD(0.0)],"derivedFrom":[subQ1,subQ0]});Q186=makeQuery(id+"F0.imprint","IMPRINT",FACE,{"disambiguationData":[TD([[makeQuery(id+"F0.imprint","IMPRINT",EDGE,{"disambiguationData":[TD([[subQ2,1.0]])],"derivedFrom":subQ1}),1.0]])]});}
            var Q187;
            {var subQ0=sQuery(id+"F0.wireOp",EDGE,"E4.32.0");var subQ1=sQuery(id+"F0.wireOp",EDGE,"E0");var subQ2=makeQuery(id+"F0.imprint","INTERSECT",VERTEX,{"disambiguationData":[OD(0.0)],"derivedFrom":[subQ1,subQ0]});Q187=makeQuery(id+"F0.imprint","IMPRINT",FACE,{"disambiguationData":[TD([[makeQuery(id+"F0.imprint","IMPRINT",EDGE,{"disambiguationData":[TD([[subQ2,1.0]])],"derivedFrom":subQ1}),1.0]])]});}
            var Q188;
            {var subQ0=sQuery(id+"F0.wireOp",EDGE,"E4.38.0");var subQ1=sQuery(id+"F0.wireOp",EDGE,"E0");var subQ2=makeQuery(id+"F0.imprint","INTERSECT",VERTEX,{"disambiguationData":[OD(1.0)],"derivedFrom":[subQ1,subQ0]});Q188=makeQuery(id+"F0.imprint","IMPRINT",FACE,{"disambiguationData":[TD([[makeQuery(id+"F0.imprint","IMPRINT",EDGE,{"disambiguationData":[TD([[subQ2,1.0]])],"derivedFrom":subQ1}),-1.0]])]});}
            var Q189;
            {var subQ0=sQuery(id+"F0.wireOp",EDGE,"E4.29.2");var subQ1=sQuery(id+"F0.wireOp",EDGE,"E0");var subQ2=makeQuery(id+"F0.imprint","INTERSECT",VERTEX,{"derivedFrom":[subQ1,subQ0]});Q189=makeQuery(id+"F0.imprint","IMPRINT",FACE,{"disambiguationData":[TD([[makeQuery(id+"F0.imprint","IMPRINT",EDGE,{"disambiguationData":[TD([[subQ2,-1.0]])],"derivedFrom":subQ1}),-1.0]])]});}
            var Q190;
            {var subQ0=sQuery(id+"F0.wireOp",EDGE,"E4.21.0");var subQ1=sQuery(id+"F0.wireOp",EDGE,"E0");var subQ2=makeQuery(id+"F0.imprint","INTERSECT",VERTEX,{"disambiguationData":[OD(0.0)],"derivedFrom":[subQ1,subQ0]});Q190=makeQuery(id+"F0.imprint","IMPRINT",FACE,{"disambiguationData":[TD([[makeQuery(id+"F0.imprint","IMPRINT",EDGE,{"disambiguationData":[TD([[subQ2,1.0]])],"derivedFrom":subQ1}),1.0]])]});}
            var Q191;
            {var subQ0=sQuery(id+"F0.wireOp",EDGE,"E4.11.0");var subQ1=sQuery(id+"F0.wireOp",EDGE,"E0");var subQ2=makeQuery(id+"F0.imprint","INTERSECT",VERTEX,{"disambiguationData":[OD(0.0)],"derivedFrom":[subQ1,subQ0]});Q191=makeQuery(id+"F0.imprint","IMPRINT",FACE,{"disambiguationData":[TD([[makeQuery(id+"F0.imprint","IMPRINT",EDGE,{"disambiguationData":[TD([[subQ2,1.0]])],"derivedFrom":subQ1}),1.0]])]});}
            var Q192;
            {var subQ0=sQuery(id+"F0.wireOp",EDGE,"E4.27.0");var subQ1=sQuery(id+"F0.wireOp",EDGE,"E0");var subQ2=makeQuery(id+"F0.imprint","INTERSECT",VERTEX,{"disambiguationData":[OD(0.0)],"derivedFrom":[subQ1,subQ0]});Q192=makeQuery(id+"F0.imprint","IMPRINT",FACE,{"disambiguationData":[TD([[makeQuery(id+"F0.imprint","IMPRINT",EDGE,{"disambiguationData":[TD([[subQ2,1.0]])],"derivedFrom":subQ1}),1.0]])]});}
            var Q193;
            {var subQ0=sQuery(id+"F0.wireOp",EDGE,"E4.19.2");var subQ1=sQuery(id+"F0.wireOp",EDGE,"E0");var subQ2=makeQuery(id+"F0.imprint","INTERSECT",VERTEX,{"derivedFrom":[subQ1,subQ0]});Q193=makeQuery(id+"F0.imprint","IMPRINT",FACE,{"disambiguationData":[TD([[makeQuery(id+"F0.imprint","IMPRINT",EDGE,{"disambiguationData":[TD([[subQ2,-1.0]])],"derivedFrom":subQ1}),-1.0]])]});}
            var Q194;
            {var subQ0=sQuery(id+"F0.wireOp",EDGE,"E4.25.0");var subQ1=sQuery(id+"F0.wireOp",EDGE,"E0");var subQ2=makeQuery(id+"F0.imprint","INTERSECT",VERTEX,{"disambiguationData":[OD(0.0)],"derivedFrom":[subQ1,subQ0]});Q194=makeQuery(id+"F0.imprint","IMPRINT",FACE,{"disambiguationData":[TD([[makeQuery(id+"F0.imprint","IMPRINT",EDGE,{"disambiguationData":[TD([[subQ2,1.0]])],"derivedFrom":subQ1}),1.0]])]});}
            var Q195;
            {var subQ0=sQuery(id+"F0.wireOp",EDGE,"E4.23.0");var subQ1=sQuery(id+"F0.wireOp",EDGE,"E0");var subQ2=makeQuery(id+"F0.imprint","INTERSECT",VERTEX,{"disambiguationData":[OD(0.0)],"derivedFrom":[subQ1,subQ0]});Q195=makeQuery(id+"F0.imprint","IMPRINT",FACE,{"disambiguationData":[TD([[makeQuery(id+"F0.imprint","IMPRINT",EDGE,{"disambiguationData":[TD([[subQ2,1.0]])],"derivedFrom":subQ1}),1.0]])]});}
            var Q196;
            {var subQ0=sQuery(id+"F0.wireOp",EDGE,"E4.39.2");var subQ1=sQuery(id+"F0.wireOp",EDGE,"E0");var subQ2=makeQuery(id+"F0.imprint","INTERSECT",VERTEX,{"derivedFrom":[subQ1,subQ0]});Q196=makeQuery(id+"F0.imprint","IMPRINT",FACE,{"disambiguationData":[TD([[makeQuery(id+"F0.imprint","IMPRINT",EDGE,{"disambiguationData":[TD([[subQ2,-1.0]])],"derivedFrom":subQ1}),-1.0]])]});}
            var Q197;
            {var subQ0=sQuery(id+"F0.wireOp",EDGE,"E4.28.2");var subQ1=sQuery(id+"F0.wireOp",EDGE,"E0");var subQ2=makeQuery(id+"F0.imprint","INTERSECT",VERTEX,{"derivedFrom":[subQ1,subQ0]});Q197=makeQuery(id+"F0.imprint","IMPRINT",FACE,{"disambiguationData":[TD([[makeQuery(id+"F0.imprint","IMPRINT",EDGE,{"disambiguationData":[TD([[subQ2,-1.0]])],"derivedFrom":subQ1}),-1.0]])]});}
            var Q198;
            {var subQ0=sQuery(id+"F0.wireOp",EDGE,"E4.11.0");var subQ1=sQuery(id+"F0.wireOp",EDGE,"E0");var subQ2=makeQuery(id+"F0.imprint","INTERSECT",VERTEX,{"disambiguationData":[OD(1.0)],"derivedFrom":[subQ1,subQ0]});Q198=makeQuery(id+"F0.imprint","IMPRINT",FACE,{"disambiguationData":[TD([[makeQuery(id+"F0.imprint","IMPRINT",EDGE,{"disambiguationData":[TD([[subQ2,1.0]])],"derivedFrom":subQ1}),-1.0]])]});}
            var Q199;
            {var subQ0=sQuery(id+"F0.wireOp",EDGE,"E4.2.0");var subQ1=sQuery(id+"F0.wireOp",EDGE,"E0");var subQ2=makeQuery(id+"F0.imprint","INTERSECT",VERTEX,{"disambiguationData":[OD(0.0)],"derivedFrom":[subQ1,subQ0]});Q199=makeQuery(id+"F0.imprint","IMPRINT",FACE,{"disambiguationData":[TD([[makeQuery(id+"F0.imprint","IMPRINT",EDGE,{"disambiguationData":[TD([[subQ2,1.0]])],"derivedFrom":subQ1}),1.0]])]});}
            var Q200;
            {var subQ0=sQuery(id+"F0.wireOp",EDGE,"E4.17.2");var subQ1=sQuery(id+"F0.wireOp",EDGE,"E0");var subQ2=makeQuery(id+"F0.imprint","INTERSECT",VERTEX,{"derivedFrom":[subQ1,subQ0]});Q200=makeQuery(id+"F0.imprint","IMPRINT",FACE,{"disambiguationData":[TD([[makeQuery(id+"F0.imprint","IMPRINT",EDGE,{"disambiguationData":[TD([[subQ2,-1.0]])],"derivedFrom":subQ1}),-1.0]])]});}
            extrude(context, id + "F1", {"entities" : qUnion([Q0, Q1, Q2, Q3, Q4, Q5, Q6, Q7, Q8, Q9, Q10, Q11, Q12, Q13, Q14, Q15, Q16, Q17, Q18, Q19, Q20, Q21, Q22, Q23, Q24, Q25, Q26, Q27, Q28, Q29, Q30, Q31, Q32, Q33, Q34, Q35, Q36, Q37, Q38, Q39, Q40, Q41, Q42, Q43, Q44, Q45, Q46, Q47, Q48, Q49, Q50, Q51, Q52, Q53, Q54, Q55, Q56, Q57, Q58, Q59, Q60, Q61, Q62, Q63, Q64, Q65, Q66, Q67, Q68, Q69, Q70, Q71, Q72, Q73, Q74, Q75, Q76, Q77, Q78, Q79, Q80, Q81, Q82, Q83, Q84, Q85, Q86, Q87, Q88, Q89, Q90, Q91, Q92, Q93, Q94, Q95, Q96, Q97, Q98, Q99, Q100, Q101, Q102, Q103, Q104, Q105, Q106, Q107, Q108, Q109, Q110, Q111, Q112, Q113, Q114, Q115, Q116, Q117, Q118, Q119, Q120, Q121, Q122, Q123, Q124, Q125, Q126, Q127, Q128, Q129, Q130, Q131, Q132, Q133, Q134, Q135, Q136, Q137, Q138, Q139, Q140, Q141, Q142, Q143, Q144, Q145, Q146, Q147, Q148, Q149, Q150, Q151, Q152, Q153, Q154, Q155, Q156, Q157, Q158, Q159, Q160, Q161, Q162, Q163, Q164, Q165, Q166, Q167, Q168, Q169, Q170, Q171, Q172, Q173, Q174, Q175, Q176, Q177, Q178, Q179, Q180, Q181, Q182, Q183, Q184, Q185, Q186, Q187, Q188, Q189, Q190, Q191, Q192, Q193, Q194, Q195, Q196, Q197, Q198, Q199, Q200]), "depth" : 11 * mm, "offsetDistance" : 25 * mm});
        }
        {
            var Q0;
            Q0=makeQuery(id+"F1.opExtrude","CAP_FACE",FACE,{"disambiguationData":[OSD([sQuery(id+"F0.wireOp",EDGE,"E0"),sQuery(id+"F0.wireOp",EDGE,"E1"),sQuery(id+"F0.wireOp",EDGE,"E2"),sQuery(id+"F0.wireOp",EDGE,"E3"),sQuery(id+"F0.wireOp",EDGE,"E4.1.0"),sQuery(id+"F0.wireOp",EDGE,"E4.1.1"),sQuery(id+"F0.wireOp",EDGE,"E4.1.2"),sQuery(id+"F0.wireOp",EDGE,"E4.2.0"),sQuery(id+"F0.wireOp",EDGE,"E4.2.1"),sQuery(id+"F0.wireOp",EDGE,"E4.2.2"),sQuery(id+"F0.wireOp",EDGE,"E4.3.0"),sQuery(id+"F0.wireOp",EDGE,"E4.3.1"),sQuery(id+"F0.wireOp",EDGE,"E4.3.2"),sQuery(id+"F0.wireOp",EDGE,"E4.4.0"),sQuery(id+"F0.wireOp",EDGE,"E4.4.1"),sQuery(id+"F0.wireOp",EDGE,"E4.4.2"),sQuery(id+"F0.wireOp",EDGE,"E4.5.0"),sQuery(id+"F0.wireOp",EDGE,"E4.5.1"),sQuery(id+"F0.wireOp",EDGE,"E4.5.2"),sQuery(id+"F0.wireOp",EDGE,"E4.6.0"),sQuery(id+"F0.wireOp",EDGE,"E4.6.1"),sQuery(id+"F0.wireOp",EDGE,"E4.6.2"),sQuery(id+"F0.wireOp",EDGE,"E4.7.0"),sQuery(id+"F0.wireOp",EDGE,"E4.7.1"),sQuery(id+"F0.wireOp",EDGE,"E4.7.2"),sQuery(id+"F0.wireOp",EDGE,"E4.8.0"),sQuery(id+"F0.wireOp",EDGE,"E4.8.1"),sQuery(id+"F0.wireOp",EDGE,"E4.8.2"),sQuery(id+"F0.wireOp",EDGE,"E4.9.0"),sQuery(id+"F0.wireOp",EDGE,"E4.9.1"),sQuery(id+"F0.wireOp",EDGE,"E4.9.2"),sQuery(id+"F0.wireOp",EDGE,"E4.10.0"),sQuery(id+"F0.wireOp",EDGE,"E4.10.1"),sQuery(id+"F0.wireOp",EDGE,"E4.10.2"),sQuery(id+"F0.wireOp",EDGE,"E4.11.0"),sQuery(id+"F0.wireOp",EDGE,"E4.11.1"),sQuery(id+"F0.wireOp",EDGE,"E4.11.2"),sQuery(id+"F0.wireOp",EDGE,"E4.12.0"),sQuery(id+"F0.wireOp",EDGE,"E4.12.1"),sQuery(id+"F0.wireOp",EDGE,"E4.12.2"),sQuery(id+"F0.wireOp",EDGE,"E4.13.0"),sQuery(id+"F0.wireOp",EDGE,"E4.13.1"),sQuery(id+"F0.wireOp",EDGE,"E4.13.2"),sQuery(id+"F0.wireOp",EDGE,"E4.14.0"),sQuery(id+"F0.wireOp",EDGE,"E4.14.1"),sQuery(id+"F0.wireOp",EDGE,"E4.14.2"),sQuery(id+"F0.wireOp",EDGE,"E4.15.0"),sQuery(id+"F0.wireOp",EDGE,"E4.15.1"),sQuery(id+"F0.wireOp",EDGE,"E4.15.2"),sQuery(id+"F0.wireOp",EDGE,"E4.16.0"),sQuery(id+"F0.wireOp",EDGE,"E4.16.1"),sQuery(id+"F0.wireOp",EDGE,"E4.16.2"),sQuery(id+"F0.wireOp",EDGE,"E4.17.0"),sQuery(id+"F0.wireOp",EDGE,"E4.17.1"),sQuery(id+"F0.wireOp",EDGE,"E4.17.2"),sQuery(id+"F0.wireOp",EDGE,"E4.18.0"),sQuery(id+"F0.wireOp",EDGE,"E4.18.1"),sQuery(id+"F0.wireOp",EDGE,"E4.18.2"),sQuery(id+"F0.wireOp",EDGE,"E4.19.0"),sQuery(id+"F0.wireOp",EDGE,"E4.19.1"),sQuery(id+"F0.wireOp",EDGE,"E4.19.2"),sQuery(id+"F0.wireOp",EDGE,"E4.20.0"),sQuery(id+"F0.wireOp",EDGE,"E4.20.1"),sQuery(id+"F0.wireOp",EDGE,"E4.20.2"),sQuery(id+"F0.wireOp",EDGE,"E4.21.0"),sQuery(id+"F0.wireOp",EDGE,"E4.21.1"),sQuery(id+"F0.wireOp",EDGE,"E4.21.2"),sQuery(id+"F0.wireOp",EDGE,"E4.22.0"),sQuery(id+"F0.wireOp",EDGE,"E4.22.1"),sQuery(id+"F0.wireOp",EDGE,"E4.22.2"),sQuery(id+"F0.wireOp",EDGE,"E4.23.0"),sQuery(id+"F0.wireOp",EDGE,"E4.23.1"),sQuery(id+"F0.wireOp",EDGE,"E4.23.2"),sQuery(id+"F0.wireOp",EDGE,"E4.24.0"),sQuery(id+"F0.wireOp",EDGE,"E4.24.1"),sQuery(id+"F0.wireOp",EDGE,"E4.24.2"),sQuery(id+"F0.wireOp",EDGE,"E4.25.0"),sQuery(id+"F0.wireOp",EDGE,"E4.25.1"),sQuery(id+"F0.wireOp",EDGE,"E4.25.2"),sQuery(id+"F0.wireOp",EDGE,"E4.26.0"),sQuery(id+"F0.wireOp",EDGE,"E4.26.1"),sQuery(id+"F0.wireOp",EDGE,"E4.26.2"),sQuery(id+"F0.wireOp",EDGE,"E4.27.0"),sQuery(id+"F0.wireOp",EDGE,"E4.27.1"),sQuery(id+"F0.wireOp",EDGE,"E4.27.2"),sQuery(id+"F0.wireOp",EDGE,"E4.28.0"),sQuery(id+"F0.wireOp",EDGE,"E4.28.1"),sQuery(id+"F0.wireOp",EDGE,"E4.28.2"),sQuery(id+"F0.wireOp",EDGE,"E4.29.0"),sQuery(id+"F0.wireOp",EDGE,"E4.29.1"),sQuery(id+"F0.wireOp",EDGE,"E4.29.2"),sQuery(id+"F0.wireOp",EDGE,"E4.30.0"),sQuery(id+"F0.wireOp",EDGE,"E4.30.1"),sQuery(id+"F0.wireOp",EDGE,"E4.30.2"),sQuery(id+"F0.wireOp",EDGE,"E4.31.0"),sQuery(id+"F0.wireOp",EDGE,"E4.31.1"),sQuery(id+"F0.wireOp",EDGE,"E4.31.2"),sQuery(id+"F0.wireOp",EDGE,"E4.32.0"),sQuery(id+"F0.wireOp",EDGE,"E4.32.1"),sQuery(id+"F0.wireOp",EDGE,"E4.32.2"),sQuery(id+"F0.wireOp",EDGE,"E4.33.0"),sQuery(id+"F0.wireOp",EDGE,"E4.33.1"),sQuery(id+"F0.wireOp",EDGE,"E4.33.2"),sQuery(id+"F0.wireOp",EDGE,"E4.34.0"),sQuery(id+"F0.wireOp",EDGE,"E4.34.1"),sQuery(id+"F0.wireOp",EDGE,"E4.34.2"),sQuery(id+"F0.wireOp",EDGE,"E4.35.0"),sQuery(id+"F0.wireOp",EDGE,"E4.35.1"),sQuery(id+"F0.wireOp",EDGE,"E4.35.2"),sQuery(id+"F0.wireOp",EDGE,"E4.36.0"),sQuery(id+"F0.wireOp",EDGE,"E4.36.1"),sQuery(id+"F0.wireOp",EDGE,"E4.36.2"),sQuery(id+"F0.wireOp",EDGE,"E4.37.0"),sQuery(id+"F0.wireOp",EDGE,"E4.37.1"),sQuery(id+"F0.wireOp",EDGE,"E4.37.2"),sQuery(id+"F0.wireOp",EDGE,"E4.38.0"),sQuery(id+"F0.wireOp",EDGE,"E4.38.1"),sQuery(id+"F0.wireOp",EDGE,"E4.38.2"),sQuery(id+"F0.wireOp",EDGE,"E4.39.0"),sQuery(id+"F0.wireOp",EDGE,"E4.39.1"),sQuery(id+"F0.wireOp",EDGE,"E4.39.2")])],"isStart":true});
            var sketch = newSketch(context, id + "F2", { "sketchPlane" : qUnion([Q0])});
            skCircle(sketch, "E5", {"center": v(0, 0) * mm, "radius": 34 * mm});
            skSolve(sketch);
        }
        {
            var Q0;
            Q0=makeQuery(id+"F1.opExtrude","CAP_FACE",FACE,{"disambiguationData":[OSD([sQuery(id+"F0.wireOp",EDGE,"E0"),sQuery(id+"F0.wireOp",EDGE,"E1"),sQuery(id+"F0.wireOp",EDGE,"E2"),sQuery(id+"F0.wireOp",EDGE,"E3"),sQuery(id+"F0.wireOp",EDGE,"E4.1.0"),sQuery(id+"F0.wireOp",EDGE,"E4.1.1"),sQuery(id+"F0.wireOp",EDGE,"E4.1.2"),sQuery(id+"F0.wireOp",EDGE,"E4.2.0"),sQuery(id+"F0.wireOp",EDGE,"E4.2.1"),sQuery(id+"F0.wireOp",EDGE,"E4.2.2"),sQuery(id+"F0.wireOp",EDGE,"E4.3.0"),sQuery(id+"F0.wireOp",EDGE,"E4.3.1"),sQuery(id+"F0.wireOp",EDGE,"E4.3.2"),sQuery(id+"F0.wireOp",EDGE,"E4.4.0"),sQuery(id+"F0.wireOp",EDGE,"E4.4.1"),sQuery(id+"F0.wireOp",EDGE,"E4.4.2"),sQuery(id+"F0.wireOp",EDGE,"E4.5.0"),sQuery(id+"F0.wireOp",EDGE,"E4.5.1"),sQuery(id+"F0.wireOp",EDGE,"E4.5.2"),sQuery(id+"F0.wireOp",EDGE,"E4.6.0"),sQuery(id+"F0.wireOp",EDGE,"E4.6.1"),sQuery(id+"F0.wireOp",EDGE,"E4.6.2"),sQuery(id+"F0.wireOp",EDGE,"E4.7.0"),sQuery(id+"F0.wireOp",EDGE,"E4.7.1"),sQuery(id+"F0.wireOp",EDGE,"E4.7.2"),sQuery(id+"F0.wireOp",EDGE,"E4.8.0"),sQuery(id+"F0.wireOp",EDGE,"E4.8.1"),sQuery(id+"F0.wireOp",EDGE,"E4.8.2"),sQuery(id+"F0.wireOp",EDGE,"E4.9.0"),sQuery(id+"F0.wireOp",EDGE,"E4.9.1"),sQuery(id+"F0.wireOp",EDGE,"E4.9.2"),sQuery(id+"F0.wireOp",EDGE,"E4.10.0"),sQuery(id+"F0.wireOp",EDGE,"E4.10.1"),sQuery(id+"F0.wireOp",EDGE,"E4.10.2"),sQuery(id+"F0.wireOp",EDGE,"E4.11.0"),sQuery(id+"F0.wireOp",EDGE,"E4.11.1"),sQuery(id+"F0.wireOp",EDGE,"E4.11.2"),sQuery(id+"F0.wireOp",EDGE,"E4.12.0"),sQuery(id+"F0.wireOp",EDGE,"E4.12.1"),sQuery(id+"F0.wireOp",EDGE,"E4.12.2"),sQuery(id+"F0.wireOp",EDGE,"E4.13.0"),sQuery(id+"F0.wireOp",EDGE,"E4.13.1"),sQuery(id+"F0.wireOp",EDGE,"E4.13.2"),sQuery(id+"F0.wireOp",EDGE,"E4.14.0"),sQuery(id+"F0.wireOp",EDGE,"E4.14.1"),sQuery(id+"F0.wireOp",EDGE,"E4.14.2"),sQuery(id+"F0.wireOp",EDGE,"E4.15.0"),sQuery(id+"F0.wireOp",EDGE,"E4.15.1"),sQuery(id+"F0.wireOp",EDGE,"E4.15.2"),sQuery(id+"F0.wireOp",EDGE,"E4.16.0"),sQuery(id+"F0.wireOp",EDGE,"E4.16.1"),sQuery(id+"F0.wireOp",EDGE,"E4.16.2"),sQuery(id+"F0.wireOp",EDGE,"E4.17.0"),sQuery(id+"F0.wireOp",EDGE,"E4.17.1"),sQuery(id+"F0.wireOp",EDGE,"E4.17.2"),sQuery(id+"F0.wireOp",EDGE,"E4.18.0"),sQuery(id+"F0.wireOp",EDGE,"E4.18.1"),sQuery(id+"F0.wireOp",EDGE,"E4.18.2"),sQuery(id+"F0.wireOp",EDGE,"E4.19.0"),sQuery(id+"F0.wireOp",EDGE,"E4.19.1"),sQuery(id+"F0.wireOp",EDGE,"E4.19.2"),sQuery(id+"F0.wireOp",EDGE,"E4.20.0"),sQuery(id+"F0.wireOp",EDGE,"E4.20.1"),sQuery(id+"F0.wireOp",EDGE,"E4.20.2"),sQuery(id+"F0.wireOp",EDGE,"E4.21.0"),sQuery(id+"F0.wireOp",EDGE,"E4.21.1"),sQuery(id+"F0.wireOp",EDGE,"E4.21.2"),sQuery(id+"F0.wireOp",EDGE,"E4.22.0"),sQuery(id+"F0.wireOp",EDGE,"E4.22.1"),sQuery(id+"F0.wireOp",EDGE,"E4.22.2"),sQuery(id+"F0.wireOp",EDGE,"E4.23.0"),sQuery(id+"F0.wireOp",EDGE,"E4.23.1"),sQuery(id+"F0.wireOp",EDGE,"E4.23.2"),sQuery(id+"F0.wireOp",EDGE,"E4.24.0"),sQuery(id+"F0.wireOp",EDGE,"E4.24.1"),sQuery(id+"F0.wireOp",EDGE,"E4.24.2"),sQuery(id+"F0.wireOp",EDGE,"E4.25.0"),sQuery(id+"F0.wireOp",EDGE,"E4.25.1"),sQuery(id+"F0.wireOp",EDGE,"E4.25.2"),sQuery(id+"F0.wireOp",EDGE,"E4.26.0"),sQuery(id+"F0.wireOp",EDGE,"E4.26.1"),sQuery(id+"F0.wireOp",EDGE,"E4.26.2"),sQuery(id+"F0.wireOp",EDGE,"E4.27.0"),sQuery(id+"F0.wireOp",EDGE,"E4.27.1"),sQuery(id+"F0.wireOp",EDGE,"E4.27.2"),sQuery(id+"F0.wireOp",EDGE,"E4.28.0"),sQuery(id+"F0.wireOp",EDGE,"E4.28.1"),sQuery(id+"F0.wireOp",EDGE,"E4.28.2"),sQuery(id+"F0.wireOp",EDGE,"E4.29.0"),sQuery(id+"F0.wireOp",EDGE,"E4.29.1"),sQuery(id+"F0.wireOp",EDGE,"E4.29.2"),sQuery(id+"F0.wireOp",EDGE,"E4.30.0"),sQuery(id+"F0.wireOp",EDGE,"E4.30.1"),sQuery(id+"F0.wireOp",EDGE,"E4.30.2"),sQuery(id+"F0.wireOp",EDGE,"E4.31.0"),sQuery(id+"F0.wireOp",EDGE,"E4.31.1"),sQuery(id+"F0.wireOp",EDGE,"E4.31.2"),sQuery(id+"F0.wireOp",EDGE,"E4.32.0"),sQuery(id+"F0.wireOp",EDGE,"E4.32.1"),sQuery(id+"F0.wireOp",EDGE,"E4.32.2"),sQuery(id+"F0.wireOp",EDGE,"E4.33.0"),sQuery(id+"F0.wireOp",EDGE,"E4.33.1"),sQuery(id+"F0.wireOp",EDGE,"E4.33.2"),sQuery(id+"F0.wireOp",EDGE,"E4.34.0"),sQuery(id+"F0.wireOp",EDGE,"E4.34.1"),sQuery(id+"F0.wireOp",EDGE,"E4.34.2"),sQuery(id+"F0.wireOp",EDGE,"E4.35.0"),sQuery(id+"F0.wireOp",EDGE,"E4.35.1"),sQuery(id+"F0.wireOp",EDGE,"E4.35.2"),sQuery(id+"F0.wireOp",EDGE,"E4.36.0"),sQuery(id+"F0.wireOp",EDGE,"E4.36.1"),sQuery(id+"F0.wireOp",EDGE,"E4.36.2"),sQuery(id+"F0.wireOp",EDGE,"E4.37.0"),sQuery(id+"F0.wireOp",EDGE,"E4.37.1"),sQuery(id+"F0.wireOp",EDGE,"E4.37.2"),sQuery(id+"F0.wireOp",EDGE,"E4.38.0"),sQuery(id+"F0.wireOp",EDGE,"E4.38.1"),sQuery(id+"F0.wireOp",EDGE,"E4.38.2"),sQuery(id+"F0.wireOp",EDGE,"E4.39.0"),sQuery(id+"F0.wireOp",EDGE,"E4.39.1"),sQuery(id+"F0.wireOp",EDGE,"E4.39.2")])],"isStart":false});
            var sketch = newSketch(context, id + "F3", { "sketchPlane" : qUnion([Q0])});
            skCircle(sketch, "E6", {"center": v(0, 0) * mm, "radius": 34 * mm});
            skSolve(sketch);
        }
        {
            var Q0;
            Q0=makeQuery(id+"F3.imprint","IMPRINT",FACE,{"disambiguationData":[TD([[makeQuery(id+"F3.imprint","IMPRINT",EDGE,{"derivedFrom":makeQuery(id+"F1.opExtrude","CAP_EDGE",EDGE,{"disambiguationData":[OSD([sQuery(id+"F0.wireOp",EDGE,"E1")])],"isStart":false})}),1.0]])]});
            var Q1;
            Q1=makeQuery(id+"F3.imprint","IMPRINT",FACE,{"disambiguationData":[TD([[makeQuery(id+"F3.imprint","IMPRINT",EDGE,{"derivedFrom":sQuery(id+"F3.wireOp",EDGE,"E6")}),1.0]])]});
            extrude(context, id + "F4", {"entities" : qUnion([Q0, Q1]), "operationType" : NewBodyOperationType.ADD, "depth" : 2 * mm, "offsetDistance" : 25 * mm});
        }
        {
            var Q0;
            Q0=makeQuery(id+"F2.imprint","IMPRINT",FACE,{"disambiguationData":[TD([[makeQuery(id+"F2.imprint","IMPRINT",EDGE,{"derivedFrom":sQuery(id+"F2.wireOp",EDGE,"E5")}),1.0]])]});
            var Q1;
            Q1=makeQuery(id+"F2.imprint","IMPRINT",FACE,{"disambiguationData":[TD([[makeQuery(id+"F2.imprint","IMPRINT",EDGE,{"derivedFrom":makeQuery(id+"F1.opExtrude","CAP_EDGE",EDGE,{"disambiguationData":[OSD([sQuery(id+"F0.wireOp",EDGE,"E1")])],"isStart":true})}),-1.0]])]});
            extrude(context, id + "F5", {"entities" : qUnion([Q0, Q1]), "operationType" : NewBodyOperationType.ADD, "oppositeDirection" : true, "depth" : 2 * mm, "offsetDistance" : 25 * mm});
        }
        {
            var Q0;
            Q0=makeQuery(id+"F4.opExtrude","CAP_FACE",FACE,{"disambiguationData":[OSD([sQuery(id+"F3.wireOp",EDGE,"E6")])],"isStart":false});
            var sketch = newSketch(context, id + "F6", { "sketchPlane" : qUnion([Q0])});
            skCircle(sketch, "E7", {"center": v(0, 0) * mm, "radius": 20 * mm});
            skSolve(sketch);
        }
        {
            var Q0;
            Q0=qSketchRegion(id+"F6",true);
            extrude(context, id + "F7", {"entities" : qUnion([Q0]), "operationType" : NewBodyOperationType.ADD, "depth" : 12 * mm, "offsetDistance" : 25 * mm});
        }
        {
            var Q0;
            Q0=makeQuery(id+"F5.boolean.opBoolean","MERGE",FACE,{"derivedFrom":[makeQuery(id+"F1.opExtrude","CAP_FACE",FACE,{"disambiguationData":[OSD([sQuery(id+"F0.wireOp",EDGE,"E0"),sQuery(id+"F0.wireOp",EDGE,"E1"),sQuery(id+"F0.wireOp",EDGE,"E2"),sQuery(id+"F0.wireOp",EDGE,"E3"),sQuery(id+"F0.wireOp",EDGE,"E4.1.0"),sQuery(id+"F0.wireOp",EDGE,"E4.1.1"),sQuery(id+"F0.wireOp",EDGE,"E4.1.2"),sQuery(id+"F0.wireOp",EDGE,"E4.2.0"),sQuery(id+"F0.wireOp",EDGE,"E4.2.1"),sQuery(id+"F0.wireOp",EDGE,"E4.2.2"),sQuery(id+"F0.wireOp",EDGE,"E4.3.0"),sQuery(id+"F0.wireOp",EDGE,"E4.3.1"),sQuery(id+"F0.wireOp",EDGE,"E4.3.2"),sQuery(id+"F0.wireOp",EDGE,"E4.4.0"),sQuery(id+"F0.wireOp",EDGE,"E4.4.1"),sQuery(id+"F0.wireOp",EDGE,"E4.4.2"),sQuery(id+"F0.wireOp",EDGE,"E4.5.0"),sQuery(id+"F0.wireOp",EDGE,"E4.5.1"),sQuery(id+"F0.wireOp",EDGE,"E4.5.2"),sQuery(id+"F0.wireOp",EDGE,"E4.6.0"),sQuery(id+"F0.wireOp",EDGE,"E4.6.1"),sQuery(id+"F0.wireOp",EDGE,"E4.6.2"),sQuery(id+"F0.wireOp",EDGE,"E4.7.0"),sQuery(id+"F0.wireOp",EDGE,"E4.7.1"),sQuery(id+"F0.wireOp",EDGE,"E4.7.2"),sQuery(id+"F0.wireOp",EDGE,"E4.8.0"),sQuery(id+"F0.wireOp",EDGE,"E4.8.1"),sQuery(id+"F0.wireOp",EDGE,"E4.8.2"),sQuery(id+"F0.wireOp",EDGE,"E4.9.0"),sQuery(id+"F0.wireOp",EDGE,"E4.9.1"),sQuery(id+"F0.wireOp",EDGE,"E4.9.2"),sQuery(id+"F0.wireOp",EDGE,"E4.10.0"),sQuery(id+"F0.wireOp",EDGE,"E4.10.1"),sQuery(id+"F0.wireOp",EDGE,"E4.10.2"),sQuery(id+"F0.wireOp",EDGE,"E4.11.0"),sQuery(id+"F0.wireOp",EDGE,"E4.11.1"),sQuery(id+"F0.wireOp",EDGE,"E4.11.2"),sQuery(id+"F0.wireOp",EDGE,"E4.12.0"),sQuery(id+"F0.wireOp",EDGE,"E4.12.1"),sQuery(id+"F0.wireOp",EDGE,"E4.12.2"),sQuery(id+"F0.wireOp",EDGE,"E4.13.0"),sQuery(id+"F0.wireOp",EDGE,"E4.13.1"),sQuery(id+"F0.wireOp",EDGE,"E4.13.2"),sQuery(id+"F0.wireOp",EDGE,"E4.14.0"),sQuery(id+"F0.wireOp",EDGE,"E4.14.1"),sQuery(id+"F0.wireOp",EDGE,"E4.14.2"),sQuery(id+"F0.wireOp",EDGE,"E4.15.0"),sQuery(id+"F0.wireOp",EDGE,"E4.15.1"),sQuery(id+"F0.wireOp",EDGE,"E4.15.2"),sQuery(id+"F0.wireOp",EDGE,"E4.16.0"),sQuery(id+"F0.wireOp",EDGE,"E4.16.1"),sQuery(id+"F0.wireOp",EDGE,"E4.16.2"),sQuery(id+"F0.wireOp",EDGE,"E4.17.0"),sQuery(id+"F0.wireOp",EDGE,"E4.17.1"),sQuery(id+"F0.wireOp",EDGE,"E4.17.2"),sQuery(id+"F0.wireOp",EDGE,"E4.18.0"),sQuery(id+"F0.wireOp",EDGE,"E4.18.1"),sQuery(id+"F0.wireOp",EDGE,"E4.18.2"),sQuery(id+"F0.wireOp",EDGE,"E4.19.0"),sQuery(id+"F0.wireOp",EDGE,"E4.19.1"),sQuery(id+"F0.wireOp",EDGE,"E4.19.2"),sQuery(id+"F0.wireOp",EDGE,"E4.20.0"),sQuery(id+"F0.wireOp",EDGE,"E4.20.1"),sQuery(id+"F0.wireOp",EDGE,"E4.20.2"),sQuery(id+"F0.wireOp",EDGE,"E4.21.0"),sQuery(id+"F0.wireOp",EDGE,"E4.21.1"),sQuery(id+"F0.wireOp",EDGE,"E4.21.2"),sQuery(id+"F0.wireOp",EDGE,"E4.22.0"),sQuery(id+"F0.wireOp",EDGE,"E4.22.1"),sQuery(id+"F0.wireOp",EDGE,"E4.22.2"),sQuery(id+"F0.wireOp",EDGE,"E4.23.0"),sQuery(id+"F0.wireOp",EDGE,"E4.23.1"),sQuery(id+"F0.wireOp",EDGE,"E4.23.2"),sQuery(id+"F0.wireOp",EDGE,"E4.24.0"),sQuery(id+"F0.wireOp",EDGE,"E4.24.1"),sQuery(id+"F0.wireOp",EDGE,"E4.24.2"),sQuery(id+"F0.wireOp",EDGE,"E4.25.0"),sQuery(id+"F0.wireOp",EDGE,"E4.25.1"),sQuery(id+"F0.wireOp",EDGE,"E4.25.2"),sQuery(id+"F0.wireOp",EDGE,"E4.26.0"),sQuery(id+"F0.wireOp",EDGE,"E4.26.1"),sQuery(id+"F0.wireOp",EDGE,"E4.26.2"),sQuery(id+"F0.wireOp",EDGE,"E4.27.0"),sQuery(id+"F0.wireOp",EDGE,"E4.27.1"),sQuery(id+"F0.wireOp",EDGE,"E4.27.2"),sQuery(id+"F0.wireOp",EDGE,"E4.28.0"),sQuery(id+"F0.wireOp",EDGE,"E4.28.1"),sQuery(id+"F0.wireOp",EDGE,"E4.28.2"),sQuery(id+"F0.wireOp",EDGE,"E4.29.0"),sQuery(id+"F0.wireOp",EDGE,"E4.29.1"),sQuery(id+"F0.wireOp",EDGE,"E4.29.2"),sQuery(id+"F0.wireOp",EDGE,"E4.30.0"),sQuery(id+"F0.wireOp",EDGE,"E4.30.1"),sQuery(id+"F0.wireOp",EDGE,"E4.30.2"),sQuery(id+"F0.wireOp",EDGE,"E4.31.0"),sQuery(id+"F0.wireOp",EDGE,"E4.31.1"),sQuery(id+"F0.wireOp",EDGE,"E4.31.2"),sQuery(id+"F0.wireOp",EDGE,"E4.32.0"),sQuery(id+"F0.wireOp",EDGE,"E4.32.1"),sQuery(id+"F0.wireOp",EDGE,"E4.32.2"),sQuery(id+"F0.wireOp",EDGE,"E4.33.0"),sQuery(id+"F0.wireOp",EDGE,"E4.33.1"),sQuery(id+"F0.wireOp",EDGE,"E4.33.2"),sQuery(id+"F0.wireOp",EDGE,"E4.34.0"),sQuery(id+"F0.wireOp",EDGE,"E4.34.1"),sQuery(id+"F0.wireOp",EDGE,"E4.34.2"),sQuery(id+"F0.wireOp",EDGE,"E4.35.0"),sQuery(id+"F0.wireOp",EDGE,"E4.35.1"),sQuery(id+"F0.wireOp",EDGE,"E4.35.2"),sQuery(id+"F0.wireOp",EDGE,"E4.36.0"),sQuery(id+"F0.wireOp",EDGE,"E4.36.1"),sQuery(id+"F0.wireOp",EDGE,"E4.36.2"),sQuery(id+"F0.wireOp",EDGE,"E4.37.0"),sQuery(id+"F0.wireOp",EDGE,"E4.37.1"),sQuery(id+"F0.wireOp",EDGE,"E4.37.2"),sQuery(id+"F0.wireOp",EDGE,"E4.38.0"),sQuery(id+"F0.wireOp",EDGE,"E4.38.1"),sQuery(id+"F0.wireOp",EDGE,"E4.38.2"),sQuery(id+"F0.wireOp",EDGE,"E4.39.0"),sQuery(id+"F0.wireOp",EDGE,"E4.39.1"),sQuery(id+"F0.wireOp",EDGE,"E4.39.2")])],"isStart":true}),makeQuery(id+"F5.opExtrude","CAP_FACE",FACE,{"disambiguationData":[OSD([sQuery(id+"F2.wireOp",EDGE,"E5")])],"isStart":true})]});
            var sketch = newSketch(context, id + "F8", { "sketchPlane" : qUnion([Q0])});
            skCircle(sketch, "E8.cCircle", {"center": v(0, 0) * mm, "radius": 13.76 * mm, "construction": true});
            skLineSegment(sketch, "E8.0", {"start": v(-16.87, 2.18) * mm, "end": v(-3.15, 16.72) * mm});
            skLineSegment(sketch, "E8.1", {"start": v(-3.15, 16.72) * mm, "end": v(14.93, 8.16) * mm});
            skLineSegment(sketch, "E8.2", {"start": v(14.93, 8.16) * mm, "end": v(12.37, -11.68) * mm});
            skLineSegment(sketch, "E8.3", {"start": v(12.37, -11.68) * mm, "end": v(-7.28, -15.38) * mm});
            skLineSegment(sketch, "E8.4", {"start": v(-7.28, -15.38) * mm, "end": v(-16.87, 2.18) * mm});
            skPoint(sketch, "E8.0.midPoint", {"position": v(-10, 9.45) * mm});
            skSolve(sketch);
        }
        {
            var Q0;
            Q0=makeQuery(id+"F8.imprint","IMPRINT",FACE,{"disambiguationData":[TD([[makeQuery(id+"F8.imprint","IMPRINT",EDGE,{"derivedFrom":sQuery(id+"F8.wireOp",EDGE,"E8.0")}),-1.0]])]});
            extrude(context, id + "F9", {"entities" : qUnion([Q0]), "operationType" : NewBodyOperationType.REMOVE, "oppositeDirection" : true, "depth" : 25 * mm, "offsetDistance" : 25 * mm});
        }
    });
